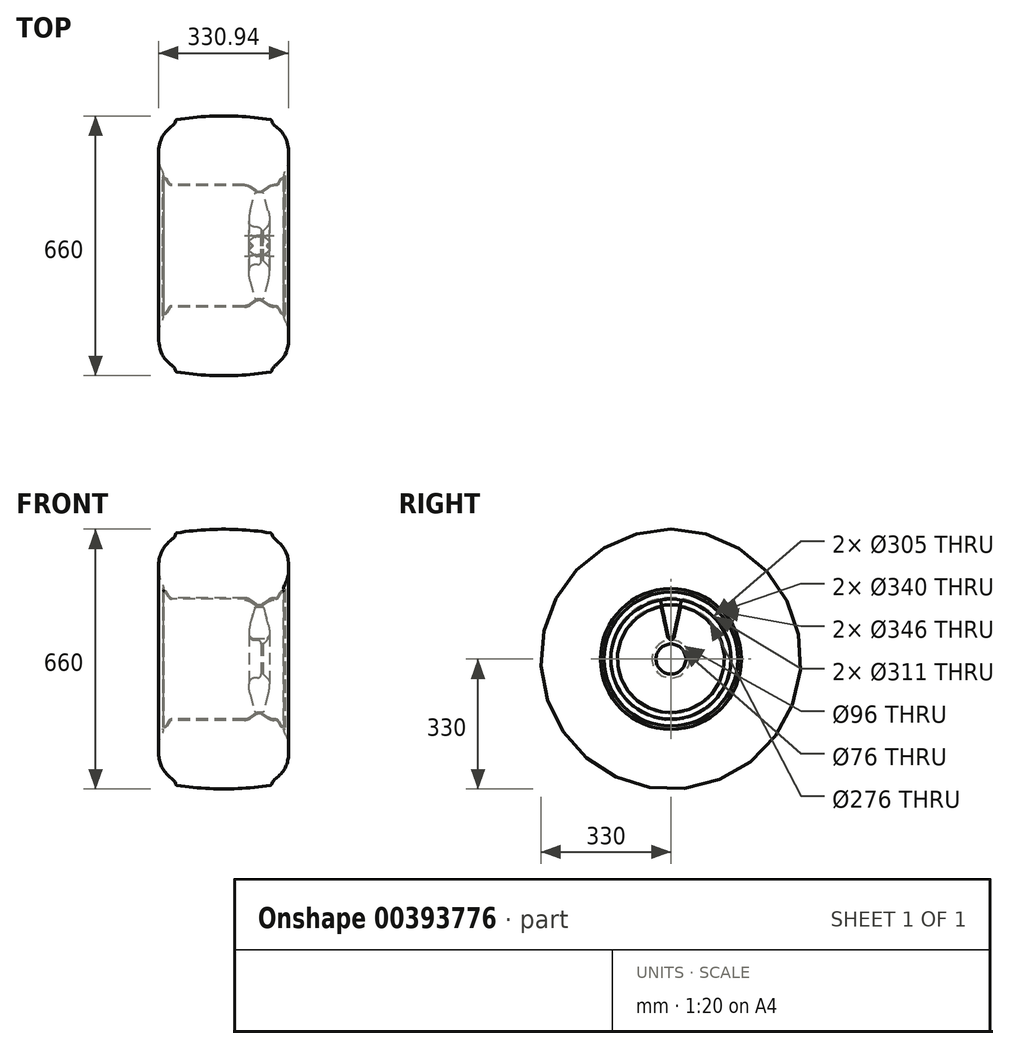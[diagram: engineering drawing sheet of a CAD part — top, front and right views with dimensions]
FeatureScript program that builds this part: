
annotation { "Feature Type Name" : "Feature", "Feature Type Description" : "" }
export const myFeature = defineFeature(function(context is Context, id is Id, definition is map)
    precondition{}
    {
        {
            var Q0;
            Q0=qCreatedBy(makeId("Front.planeOp"),FACE);
            var sketch = newSketch(context, id + "F0", { "sketchPlane" : qUnion([Q0])});
            skLineSegment(sketch, "E0", {"start": v(66.86, 147.98) * mm, "end": v(81.53, 137.71) * mm});
            skLineSegment(sketch, "E1", {"start": v(90.13, 135) * mm, "end": v(90.67, 135) * mm});
            skLineSegment(sketch, "E2", {"start": v(99.27, 137.71) * mm, "end": v(113.94, 147.98) * mm});
            skLineSegment(sketch, "E3", {"start": v(128.28, 152.5) * mm, "end": v(131.6, 152.5) * mm});
            skLineSegment(sketch, "E4", {"start": v(149.72, 170) * mm, "end": v(151.4, 170) * mm});
            skLineSegment(sketch, "E5", {"start": v(155.4, 174) * mm, "end": v(155.4, 178) * mm});
            skLineSegment(sketch, "E6", {"start": v(-149.72, 170) * mm, "end": v(-151.4, 170) * mm});
            skLineSegment(sketch, "E7", {"start": v(-155.4, 174) * mm, "end": v(-155.4, 178) * mm});
            skLineSegment(sketch, "E8", {"start": v(-131.6, 152.5) * mm, "end": v(52.52, 152.5) * mm});
            skLineSegment(sketch, "E9", {"start": v(-146.25, 167.98) * mm, "end": v(-140.28, 157.54) * mm});
            skLineSegment(sketch, "E10", {"start": v(140.28, 157.54) * mm, "end": v(146.25, 167.98) * mm});
            skPoint(sketch, "E11.visualSharp", {"position": v(155.4, 170) * mm});
            skArc(sketch, "E11.filletArc", {"start": v(151.4, 170) * mm, "mid": v(154.23, 171.17) * mm, "end": v(155.4, 174) * mm});
            skPoint(sketch, "E12.visualSharp", {"position": v(-155.4, 170) * mm});
            skArc(sketch, "E12.filletArc", {"start": v(-155.4, 174) * mm, "mid": v(-154.23, 171.17) * mm, "end": v(-151.4, 170) * mm});
            skPoint(sketch, "E13.visualSharp", {"position": v(-137.4, 152.5) * mm});
            skArc(sketch, "E13.filletArc", {"start": v(-140.28, 157.54) * mm, "mid": v(-136.62, 153.85) * mm, "end": v(-131.6, 152.5) * mm});
            skPoint(sketch, "E14.visualSharp", {"position": v(137.4, 152.5) * mm});
            skArc(sketch, "E14.filletArc", {"start": v(131.6, 152.5) * mm, "mid": v(136.62, 153.85) * mm, "end": v(140.28, 157.54) * mm});
            skPoint(sketch, "E15.visualSharp", {"position": v(-147.4, 170) * mm});
            skArc(sketch, "E15.filletArc", {"start": v(-146.25, 167.98) * mm, "mid": v(-147.71, 169.46) * mm, "end": v(-149.72, 170) * mm});
            skPoint(sketch, "E16.visualSharp", {"position": v(147.4, 170) * mm});
            skArc(sketch, "E16.filletArc", {"start": v(149.72, 170) * mm, "mid": v(147.71, 169.46) * mm, "end": v(146.25, 167.98) * mm});
            skPoint(sketch, "E17.visualSharp", {"position": v(60.4, 152.5) * mm});
            skArc(sketch, "E17.filletArc", {"start": v(66.86, 147.98) * mm, "mid": v(60.04, 151.34) * mm, "end": v(52.52, 152.5) * mm});
            skPoint(sketch, "E18.visualSharp", {"position": v(120.4, 152.5) * mm});
            skArc(sketch, "E18.filletArc", {"start": v(128.28, 152.5) * mm, "mid": v(120.76, 151.34) * mm, "end": v(113.94, 147.98) * mm});
            skPoint(sketch, "E19.visualSharp", {"position": v(95.4, 135) * mm});
            skArc(sketch, "E19.filletArc", {"start": v(90.67, 135) * mm, "mid": v(95.18, 135.7) * mm, "end": v(99.27, 137.71) * mm});
            skPoint(sketch, "E20.visualSharp", {"position": v(85.4, 135) * mm});
            skArc(sketch, "E20.filletArc", {"start": v(81.53, 137.71) * mm, "mid": v(85.62, 135.7) * mm, "end": v(90.13, 135) * mm});
            skLineSegment(sketch, "E21.0", {"start": v(152.4, 174) * mm, "end": v(152.4, 178) * mm});
            skArc(sketch, "E21.1", {"start": v(151.4, 173) * mm, "mid": v(152.1, 173.3) * mm, "end": v(152.4, 174) * mm});
            skLineSegment(sketch, "E21.2", {"start": v(149.72, 173) * mm, "end": v(151.4, 173) * mm});
            skArc(sketch, "E21.3", {"start": v(149.72, 173) * mm, "mid": v(146.2, 172.05) * mm, "end": v(143.64, 169.47) * mm});
            skLineSegment(sketch, "E21.4", {"start": v(137.67, 159.03) * mm, "end": v(143.64, 169.47) * mm});
            skArc(sketch, "E21.5", {"start": v(131.6, 155.5) * mm, "mid": v(135.11, 156.45) * mm, "end": v(137.67, 159.03) * mm});
            skLineSegment(sketch, "E21.6", {"start": v(128.28, 155.5) * mm, "end": v(131.6, 155.5) * mm});
            skArc(sketch, "E21.7", {"start": v(128.28, 155.5) * mm, "mid": v(119.86, 154.2) * mm, "end": v(112.22, 150.44) * mm});
            skLineSegment(sketch, "E21.8", {"start": v(97.55, 140.17) * mm, "end": v(112.22, 150.44) * mm});
            skArc(sketch, "E21.9", {"start": v(90.67, 138) * mm, "mid": v(94.28, 138.56) * mm, "end": v(97.55, 140.17) * mm});
            skLineSegment(sketch, "E21.10", {"start": v(90.13, 138) * mm, "end": v(90.67, 138) * mm});
            skArc(sketch, "E21.11", {"start": v(-143.64, 169.47) * mm, "mid": v(-146.2, 172.05) * mm, "end": v(-149.72, 173) * mm});
            skLineSegment(sketch, "E21.12", {"start": v(-149.72, 173) * mm, "end": v(-151.4, 173) * mm});
            skArc(sketch, "E21.13", {"start": v(-152.4, 174) * mm, "mid": v(-152.1, 173.3) * mm, "end": v(-151.4, 173) * mm});
            skLineSegment(sketch, "E21.14", {"start": v(-152.4, 174) * mm, "end": v(-152.4, 178) * mm});
            skLineSegment(sketch, "E21.15", {"start": v(-143.64, 169.47) * mm, "end": v(-137.67, 159.03) * mm});
            skArc(sketch, "E21.16", {"start": v(-137.67, 159.03) * mm, "mid": v(-135.11, 156.45) * mm, "end": v(-131.6, 155.5) * mm});
            skLineSegment(sketch, "E21.17", {"start": v(-131.6, 155.5) * mm, "end": v(52.52, 155.5) * mm});
            skArc(sketch, "E21.18", {"start": v(68.58, 150.44) * mm, "mid": v(60.94, 154.2) * mm, "end": v(52.52, 155.5) * mm});
            skLineSegment(sketch, "E21.19", {"start": v(68.58, 150.44) * mm, "end": v(83.25, 140.17) * mm});
            skArc(sketch, "E21.20", {"start": v(83.25, 140.17) * mm, "mid": v(86.52, 138.56) * mm, "end": v(90.13, 138) * mm});
            skLineSegment(sketch, "E22", {"start": v(154.4, 179) * mm, "end": v(153.4, 179) * mm});
            skLineSegment(sketch, "E23", {"start": v(-154.4, 179) * mm, "end": v(-153.4, 179) * mm});
            skPoint(sketch, "E24.visualSharp", {"position": v(-155.4, 179) * mm});
            skArc(sketch, "E24.filletArc", {"start": v(-154.4, 179) * mm, "mid": v(-155.1, 178.7) * mm, "end": v(-155.4, 178) * mm});
            skPoint(sketch, "E25.visualSharp", {"position": v(-152.4, 179) * mm});
            skArc(sketch, "E25.filletArc", {"start": v(-152.4, 178) * mm, "mid": v(-152.7, 178.7) * mm, "end": v(-153.4, 179) * mm});
            skPoint(sketch, "E26.visualSharp", {"position": v(152.4, 179) * mm});
            skArc(sketch, "E26.filletArc", {"start": v(153.4, 179) * mm, "mid": v(152.7, 178.7) * mm, "end": v(152.4, 178) * mm});
            skPoint(sketch, "E27.visualSharp", {"position": v(155.4, 179) * mm});
            skArc(sketch, "E27.filletArc", {"start": v(155.4, 178) * mm, "mid": v(155.1, 178.7) * mm, "end": v(154.4, 179) * mm});
            skLineSegment(sketch, "E28", {"start": v(-244.06, 0) * mm, "end": v(333.32, 0) * mm, "construction": true});
            skLineSegment(sketch, "E29", {"start": v(100.15, 138.32) * mm, "end": v(113.4, 88.88) * mm});
            skArc(sketch, "E30", {"start": v(113.4, 88.88) * mm, "mid": v(115.94, 76.05) * mm, "end": v(116.8, 63) * mm});
            skLineSegment(sketch, "E31", {"start": v(116.8, 63) * mm, "end": v(116.8, 94.03) * mm, "construction": true});
            skLineSegment(sketch, "E32", {"start": v(85.59, 48) * mm, "end": v(79, 48) * mm});
            skArc(sketch, "E33", {"start": v(79, 48) * mm, "mid": v(68.4, 52.4) * mm, "end": v(64, 63) * mm});
            skArc(sketch, "E34", {"start": v(64, 63) * mm, "mid": v(64.86, 76.05) * mm, "end": v(67.4, 88.88) * mm});
            skLineSegment(sketch, "E35", {"start": v(64, 63) * mm, "end": v(64, 94.03) * mm, "construction": true});
            skLineSegment(sketch, "E36", {"start": v(67.4, 88.88) * mm, "end": v(80.65, 138.32) * mm});
            skLineSegment(sketch, "E37", {"start": v(95.59, 38) * mm, "end": v(95.59, 38) * mm});
            skLineSegment(sketch, "E38", {"start": v(95.59, 38) * mm, "end": v(100.59, 38) * mm});
            skLineSegment(sketch, "E39", {"start": v(100.59, 38) * mm, "end": v(110.59, 48) * mm});
            skPoint(sketch, "E40.visualSharp", {"position": v(95.59, 48) * mm});
            skArc(sketch, "E40.filletArc", {"start": v(95.59, 38) * mm, "mid": v(92.66, 45.07) * mm, "end": v(85.59, 48) * mm});
            skArc(sketch, "E41", {"start": v(116.8, 63) * mm, "mid": v(115.19, 54.88) * mm, "end": v(110.59, 48) * mm});
            skArc(sketch, "E42", {"start": v(118.53, 320.64) * mm, "mid": v(0, 330) * mm, "end": v(-118.53, 320.64) * mm});
            skPoint(sketch, "E43.start.orphan", {"position": v(0, 330) * mm});
            skFitSpline(sketch, "E44", {"points": [v(152.4, 178) * mm, v(154.47, 187.1) * mm, v(163.17, 209.6) * mm, v(156.15, 276.43) * mm, v(126.69, 308.66) * mm, v(122.5, 320) * mm], "startDerivative": vector(0, 85.8) * mm, "endDerivative": vector(0, 123.74) * mm});
            skLineSegment(sketch, "E45", {"start": v(122.5, 320) * mm, "end": v(122.5, 293) * mm, "construction": true});
            skFitSpline(sketch, "E46", {"points": [v(-122.5, 320) * mm, v(-126.69, 308.66) * mm, v(-156.15, 276.43) * mm, v(-163.17, 209.6) * mm, v(-154.47, 187.1) * mm, v(-152.4, 178) * mm], "startDerivative": vector(0, -123.74) * mm, "endDerivative": vector(0, -85.8) * mm});
            skLineSegment(sketch, "E47", {"start": v(-122.5, 320) * mm, "end": v(-122.5, 293) * mm, "construction": true});
            skArc(sketch, "E48.filletArc", {"start": v(122.7, 316.36) * mm, "mid": v(121.32, 319.2) * mm, "end": v(118.53, 320.64) * mm});
            skArc(sketch, "E49.filletArc", {"start": v(-118.53, 320.64) * mm, "mid": v(-121.32, 319.2) * mm, "end": v(-122.7, 316.36) * mm});
            skSolve(sketch);
        }
        {
            var Q0;
            Q0=qCreatedBy(makeId("Right.planeOp"),FACE);
            var sketch = newSketch(context, id + "F1", { "sketchPlane" : qUnion([Q0])});
            skArc(sketch, "E50", {"start": v(-29.75, 149.57) * mm, "mid": v(0, 152.5) * mm, "end": v(29.75, 149.57) * mm, "construction": true});
            skLineSegment(sketch, "E51", {"start": v(-29.75, 149.57) * mm, "end": v(0, 0) * mm, "construction": true});
            skLineSegment(sketch, "E52", {"start": v(29.75, 149.57) * mm, "end": v(0, 0) * mm, "construction": true});
            skArc(sketch, "E53", {"start": v(10.34, 51.98) * mm, "mid": v(0, 53) * mm, "end": v(-10.34, 51.98) * mm, "construction": true});
            skLineSegment(sketch, "E54", {"start": v(0, 0) * mm, "end": v(-34.81, 197.43) * mm, "construction": true});
            skLineSegment(sketch, "E55", {"start": v(0, 0) * mm, "end": v(34.81, 197.43) * mm, "construction": true});
            skArc(sketch, "E56", {"start": v(26.48, 150.18) * mm, "mid": v(0, 152.5) * mm, "end": v(-26.48, 150.18) * mm});
            skLineSegment(sketch, "E57", {"start": v(0, 0) * mm, "end": v(19.74, 187.83) * mm, "construction": true});
            skLineSegment(sketch, "E58", {"start": v(0, 0) * mm, "end": v(-19.74, 187.83) * mm, "construction": true});
            skLineSegment(sketch, "E59", {"start": v(-6.78, 58.48) * mm, "end": v(-26.48, 150.18) * mm});
            skLineSegment(sketch, "E60", {"start": v(6.78, 58.48) * mm, "end": v(26.48, 150.18) * mm});
            skPoint(sketch, "E61.visualSharp", {"position": v(-5.54, 52.7) * mm});
            skArc(sketch, "E61.filletArc", {"start": v(-6.78, 58.48) * mm, "mid": v(-4.36, 54.54) * mm, "end": v(0, 53) * mm});
            skPoint(sketch, "E62.visualSharp", {"position": v(5.54, 52.7) * mm});
            skArc(sketch, "E62.filletArc", {"start": v(0, 53) * mm, "mid": v(4.36, 54.54) * mm, "end": v(6.78, 58.48) * mm});
            skSolve(sketch);
        }
        {
            var Q0;
            Q0=makeQuery(id+"F0.imprint","IMPRINT",FACE,{"disambiguationData":[TD([[makeQuery(id+"F0.imprint","IMPRINT",EDGE,{"derivedFrom":sQuery(id+"F0.wireOp",EDGE,"E3")}),1.0]])]});
            var Q1;
            Q1=sQuery(id+"F0.wireOp",EDGE,"E28");
            revolve(context, id + "F2", {"entities" : qUnion([Q0]), "axis" : qUnion([Q1]), "revolveType" : RevolveType.FULL});
        }
        {
            var Q0;
            Q0=makeQuery(id+"F0.imprint","IMPRINT",FACE,{"disambiguationData":[TD([[makeQuery(id+"F0.imprint","IMPRINT",EDGE,{"derivedFrom":sQuery(id+"F0.wireOp",EDGE,"E1")}),-1.0]])]});
            var Q1;
            Q1=sQuery(id+"F0.wireOp",EDGE,"E28");
            revolve(context, id + "F3", {"entities" : qUnion([Q0]), "axis" : qUnion([Q1]), "revolveType" : RevolveType.FULL});
        }
        {
            var Q0;
            Q0=makeQuery(id+"F1.imprint","IMPRINT",FACE,{"disambiguationData":[TD([[makeQuery(id+"F1.imprint","IMPRINT",EDGE,{"derivedFrom":sQuery(id+"F1.wireOp",EDGE,"E56")}),1.0]])]});
            extrude(context, id + "F4", {"entities" : qUnion([Q0]), "operationType" : NewBodyOperationType.REMOVE, "endBound" : BoundingType.THROUGH_ALL, "oppositeDirection" : true, "depth" : 25 * mm, "hasSecondDirection" : true, "secondDirectionBound" : SecondDirectionBoundingType.THROUGH_ALL, "secondDirectionOppositeDirection" : false, "secondDirectionDepth" : 25 * mm});
        }
        {
            var Q0;
            Q0=makeQuery(id+"F4.boolean.opBoolean","INTERSECT",EDGE,{"derivedFrom":[makeQuery(id+"F3.opRevolve","SWEPT_FACE",FACE,{"disambiguationData":[OSD([sQuery(id+"F0.wireOp",EDGE,"E34")])]}),makeQuery(id+"F4.opExtrude","SWEPT_FACE",FACE,{"disambiguationData":[OSD([sQuery(id+"F1.wireOp",EDGE,"E60")])]})]});
            var Q1;
            Q1=makeQuery(id+"F1MoAnU7Y2teXVl_2.1.F4.boolean.opBoolean","INTERSECT",EDGE,{"derivedFrom":[makeQuery(id+"F3.opRevolve","SWEPT_FACE",FACE,{"disambiguationData":[OSD([sQuery(id+"F0.wireOp",EDGE,"E34")])]}),makeQuery(id+"F1MoAnU7Y2teXVl_2.1.F4.opExtrude","SWEPT_FACE",FACE,{"disambiguationData":[OSD([sQuery(id+"F1.wireOp",EDGE,"E60")])]})]});
            var Q2;
            {var subQ0=sQuery(id+"F1.wireOp",EDGE,"E60");Q2=makeQuery(id+"F1MoAnU7Y2teXVl_2.2.F4.boolean.opBoolean","INTERSECT",EDGE,{"derivedFrom":[makeQuery(id+"F1MoAnU7Y2teXVl_2.1.F4.boolean.opBoolean","SPLIT",FACE,{"disambiguationData":[TD([makeQuery(id+"F4.boolean.opBoolean","COPY",FACE,{"derivedFrom":makeQuery(id+"F4.opExtrude","SWEPT_FACE",FACE,{"disambiguationData":[OSD([subQ0])]})})])],"derivedFrom":makeQuery(id+"F3.opRevolve","SWEPT_FACE",FACE,{"disambiguationData":[OSD([sQuery(id+"F0.wireOp",EDGE,"E34")])]})}),makeQuery(id+"F1MoAnU7Y2teXVl_2.2.F4.opExtrude","SWEPT_FACE",FACE,{"disambiguationData":[OSD([subQ0])]})]});}
            var Q3;
            {var subQ0=sQuery(id+"F1.wireOp",EDGE,"E60");var subQ3=makeQuery(id+"F4.boolean.opBoolean","COPY",FACE,{"derivedFrom":makeQuery(id+"F4.opExtrude","SWEPT_FACE",FACE,{"disambiguationData":[OSD([subQ0])]})});Q3=makeQuery(id+"F1MoAnU7Y2teXVl_2.3.F4.boolean.opBoolean","INTERSECT",EDGE,{"derivedFrom":[makeQuery(id+"F1MoAnU7Y2teXVl_2.2.F4.boolean.opBoolean","SPLIT",FACE,{"disambiguationData":[TD([subQ3])],"derivedFrom":makeQuery(id+"F1MoAnU7Y2teXVl_2.1.F4.boolean.opBoolean","SPLIT",FACE,{"disambiguationData":[TD([subQ3])],"derivedFrom":makeQuery(id+"F3.opRevolve","SWEPT_FACE",FACE,{"disambiguationData":[OSD([sQuery(id+"F0.wireOp",EDGE,"E34")])]})})}),makeQuery(id+"F1MoAnU7Y2teXVl_2.3.F4.opExtrude","SWEPT_FACE",FACE,{"disambiguationData":[OSD([subQ0])]})]});}
            var Q4;
            {var subQ0=sQuery(id+"F1.wireOp",EDGE,"E60");var subQ3=makeQuery(id+"F4.boolean.opBoolean","COPY",FACE,{"derivedFrom":makeQuery(id+"F4.opExtrude","SWEPT_FACE",FACE,{"disambiguationData":[OSD([subQ0])]})});Q4=makeQuery(id+"F1MoAnU7Y2teXVl_2.4.F4.boolean.opBoolean","INTERSECT",EDGE,{"derivedFrom":[makeQuery(id+"F1MoAnU7Y2teXVl_2.3.F4.boolean.opBoolean","SPLIT",FACE,{"disambiguationData":[TD([subQ3])],"derivedFrom":makeQuery(id+"F1MoAnU7Y2teXVl_2.2.F4.boolean.opBoolean","SPLIT",FACE,{"disambiguationData":[TD([subQ3])],"derivedFrom":makeQuery(id+"F1MoAnU7Y2teXVl_2.1.F4.boolean.opBoolean","SPLIT",FACE,{"disambiguationData":[TD([subQ3])],"derivedFrom":makeQuery(id+"F3.opRevolve","SWEPT_FACE",FACE,{"disambiguationData":[OSD([sQuery(id+"F0.wireOp",EDGE,"E34")])]})})})}),makeQuery(id+"F1MoAnU7Y2teXVl_2.4.F4.opExtrude","SWEPT_FACE",FACE,{"disambiguationData":[OSD([subQ0])]})]});}
            var Q5;
            {var subQ0=sQuery(id+"F1.wireOp",EDGE,"E60");var subQ3=makeQuery(id+"F4.boolean.opBoolean","COPY",FACE,{"derivedFrom":makeQuery(id+"F4.opExtrude","SWEPT_FACE",FACE,{"disambiguationData":[OSD([subQ0])]})});Q5=makeQuery(id+"F1MoAnU7Y2teXVl_2.5.F4.boolean.opBoolean","INTERSECT",EDGE,{"derivedFrom":[makeQuery(id+"F1MoAnU7Y2teXVl_2.4.F4.boolean.opBoolean","SPLIT",FACE,{"disambiguationData":[TD([subQ3])],"derivedFrom":makeQuery(id+"F1MoAnU7Y2teXVl_2.3.F4.boolean.opBoolean","SPLIT",FACE,{"disambiguationData":[TD([subQ3])],"derivedFrom":makeQuery(id+"F1MoAnU7Y2teXVl_2.2.F4.boolean.opBoolean","SPLIT",FACE,{"disambiguationData":[TD([subQ3])],"derivedFrom":makeQuery(id+"F1MoAnU7Y2teXVl_2.1.F4.boolean.opBoolean","SPLIT",FACE,{"disambiguationData":[TD([subQ3])],"derivedFrom":makeQuery(id+"F3.opRevolve","SWEPT_FACE",FACE,{"disambiguationData":[OSD([sQuery(id+"F0.wireOp",EDGE,"E34")])]})})})})}),makeQuery(id+"F1MoAnU7Y2teXVl_2.5.F4.opExtrude","SWEPT_FACE",FACE,{"disambiguationData":[OSD([subQ0])]})]});}
            var Q6;
            {var subQ0=sQuery(id+"F1.wireOp",EDGE,"E60");var subQ4=makeQuery(id+"F4.boolean.opBoolean","COPY",FACE,{"derivedFrom":makeQuery(id+"F4.opExtrude","SWEPT_FACE",FACE,{"disambiguationData":[OSD([subQ0])]})});Q6=makeQuery(id+"F1MoAnU7Y2teXVl_2.6.F4.boolean.opBoolean","INTERSECT",EDGE,{"derivedFrom":[makeQuery(id+"F1MoAnU7Y2teXVl_2.5.F4.boolean.opBoolean","SPLIT",FACE,{"disambiguationData":[TD([subQ4])],"derivedFrom":makeQuery(id+"F1MoAnU7Y2teXVl_2.4.F4.boolean.opBoolean","SPLIT",FACE,{"disambiguationData":[TD([subQ4])],"derivedFrom":makeQuery(id+"F1MoAnU7Y2teXVl_2.3.F4.boolean.opBoolean","SPLIT",FACE,{"disambiguationData":[TD([subQ4])],"derivedFrom":makeQuery(id+"F1MoAnU7Y2teXVl_2.2.F4.boolean.opBoolean","SPLIT",FACE,{"disambiguationData":[TD([subQ4])],"derivedFrom":makeQuery(id+"F1MoAnU7Y2teXVl_2.1.F4.boolean.opBoolean","SPLIT",FACE,{"disambiguationData":[TD([subQ4])],"derivedFrom":makeQuery(id+"F3.opRevolve","SWEPT_FACE",FACE,{"disambiguationData":[OSD([sQuery(id+"F0.wireOp",EDGE,"E34")])]})})})})})}),makeQuery(id+"F1MoAnU7Y2teXVl_2.6.F4.opExtrude","SWEPT_FACE",FACE,{"disambiguationData":[OSD([subQ0])]})]});}
            var Q7;
            {var subQ0=sQuery(id+"F1.wireOp",EDGE,"E60");var subQ3=makeQuery(id+"F4.boolean.opBoolean","COPY",FACE,{"derivedFrom":makeQuery(id+"F4.opExtrude","SWEPT_FACE",FACE,{"disambiguationData":[OSD([subQ0])]})});Q7=makeQuery(id+"F1MoAnU7Y2teXVl_2.7.F4.boolean.opBoolean","INTERSECT",EDGE,{"derivedFrom":[makeQuery(id+"F1MoAnU7Y2teXVl_2.6.F4.boolean.opBoolean","SPLIT",FACE,{"disambiguationData":[TD([subQ3])],"derivedFrom":makeQuery(id+"F1MoAnU7Y2teXVl_2.5.F4.boolean.opBoolean","SPLIT",FACE,{"disambiguationData":[TD([subQ3])],"derivedFrom":makeQuery(id+"F1MoAnU7Y2teXVl_2.4.F4.boolean.opBoolean","SPLIT",FACE,{"disambiguationData":[TD([subQ3])],"derivedFrom":makeQuery(id+"F1MoAnU7Y2teXVl_2.3.F4.boolean.opBoolean","SPLIT",FACE,{"disambiguationData":[TD([subQ3])],"derivedFrom":makeQuery(id+"F1MoAnU7Y2teXVl_2.2.F4.boolean.opBoolean","SPLIT",FACE,{"disambiguationData":[TD([subQ3])],"derivedFrom":makeQuery(id+"F1MoAnU7Y2teXVl_2.1.F4.boolean.opBoolean","SPLIT",FACE,{"disambiguationData":[TD([subQ3])],"derivedFrom":makeQuery(id+"F3.opRevolve","SWEPT_FACE",FACE,{"disambiguationData":[OSD([sQuery(id+"F0.wireOp",EDGE,"E34")])]})})})})})})}),makeQuery(id+"F1MoAnU7Y2teXVl_2.7.F4.opExtrude","SWEPT_FACE",FACE,{"disambiguationData":[OSD([subQ0])]})]});}
            var Q8;
            {var subQ0=sQuery(id+"F1.wireOp",EDGE,"E60");var subQ3=makeQuery(id+"F4.boolean.opBoolean","COPY",FACE,{"derivedFrom":makeQuery(id+"F4.opExtrude","SWEPT_FACE",FACE,{"disambiguationData":[OSD([subQ0])]})});Q8=makeQuery(id+"F1MoAnU7Y2teXVl_2.8.F4.boolean.opBoolean","INTERSECT",EDGE,{"derivedFrom":[makeQuery(id+"F1MoAnU7Y2teXVl_2.7.F4.boolean.opBoolean","SPLIT",FACE,{"disambiguationData":[TD([subQ3])],"derivedFrom":makeQuery(id+"F1MoAnU7Y2teXVl_2.6.F4.boolean.opBoolean","SPLIT",FACE,{"disambiguationData":[TD([subQ3])],"derivedFrom":makeQuery(id+"F1MoAnU7Y2teXVl_2.5.F4.boolean.opBoolean","SPLIT",FACE,{"disambiguationData":[TD([subQ3])],"derivedFrom":makeQuery(id+"F1MoAnU7Y2teXVl_2.4.F4.boolean.opBoolean","SPLIT",FACE,{"disambiguationData":[TD([subQ3])],"derivedFrom":makeQuery(id+"F1MoAnU7Y2teXVl_2.3.F4.boolean.opBoolean","SPLIT",FACE,{"disambiguationData":[TD([subQ3])],"derivedFrom":makeQuery(id+"F1MoAnU7Y2teXVl_2.2.F4.boolean.opBoolean","SPLIT",FACE,{"disambiguationData":[TD([subQ3])],"derivedFrom":makeQuery(id+"F1MoAnU7Y2teXVl_2.1.F4.boolean.opBoolean","SPLIT",FACE,{"disambiguationData":[TD([subQ3])],"derivedFrom":makeQuery(id+"F3.opRevolve","SWEPT_FACE",FACE,{"disambiguationData":[OSD([sQuery(id+"F0.wireOp",EDGE,"E34")])]})})})})})})})}),makeQuery(id+"F1MoAnU7Y2teXVl_2.8.F4.opExtrude","SWEPT_FACE",FACE,{"disambiguationData":[OSD([subQ0])]})]});}
            var Q9;
            {var subQ0=sQuery(id+"F1.wireOp",EDGE,"E60");var subQ3=makeQuery(id+"F4.boolean.opBoolean","COPY",FACE,{"derivedFrom":makeQuery(id+"F4.opExtrude","SWEPT_FACE",FACE,{"disambiguationData":[OSD([subQ0])]})});Q9=makeQuery(id+"F1MoAnU7Y2teXVl_2.9.F4.boolean.opBoolean","INTERSECT",EDGE,{"derivedFrom":[makeQuery(id+"F1MoAnU7Y2teXVl_2.8.F4.boolean.opBoolean","SPLIT",FACE,{"disambiguationData":[TD([subQ3])],"derivedFrom":makeQuery(id+"F1MoAnU7Y2teXVl_2.7.F4.boolean.opBoolean","SPLIT",FACE,{"disambiguationData":[TD([subQ3])],"derivedFrom":makeQuery(id+"F1MoAnU7Y2teXVl_2.6.F4.boolean.opBoolean","SPLIT",FACE,{"disambiguationData":[TD([subQ3])],"derivedFrom":makeQuery(id+"F1MoAnU7Y2teXVl_2.5.F4.boolean.opBoolean","SPLIT",FACE,{"disambiguationData":[TD([subQ3])],"derivedFrom":makeQuery(id+"F1MoAnU7Y2teXVl_2.4.F4.boolean.opBoolean","SPLIT",FACE,{"disambiguationData":[TD([subQ3])],"derivedFrom":makeQuery(id+"F1MoAnU7Y2teXVl_2.3.F4.boolean.opBoolean","SPLIT",FACE,{"disambiguationData":[TD([subQ3])],"derivedFrom":makeQuery(id+"F1MoAnU7Y2teXVl_2.2.F4.boolean.opBoolean","SPLIT",FACE,{"disambiguationData":[TD([subQ3])],"derivedFrom":makeQuery(id+"F1MoAnU7Y2teXVl_2.1.F4.boolean.opBoolean","SPLIT",FACE,{"disambiguationData":[TD([subQ3])],"derivedFrom":makeQuery(id+"F3.opRevolve","SWEPT_FACE",FACE,{"disambiguationData":[OSD([sQuery(id+"F0.wireOp",EDGE,"E34")])]})})})})})})})})}),makeQuery(id+"F1MoAnU7Y2teXVl_2.9.F4.opExtrude","SWEPT_FACE",FACE,{"disambiguationData":[OSD([subQ0])]})]});}
            var Q10;
            {var subQ0=sQuery(id+"F1.wireOp",EDGE,"E60");var subQ4=makeQuery(id+"F4.boolean.opBoolean","COPY",FACE,{"derivedFrom":makeQuery(id+"F4.opExtrude","SWEPT_FACE",FACE,{"disambiguationData":[OSD([subQ0])]})});Q10=makeQuery(id+"F1MoAnU7Y2teXVl_2.10.F4.boolean.opBoolean","INTERSECT",EDGE,{"derivedFrom":[makeQuery(id+"F1MoAnU7Y2teXVl_2.9.F4.boolean.opBoolean","SPLIT",FACE,{"disambiguationData":[TD([subQ4])],"derivedFrom":makeQuery(id+"F1MoAnU7Y2teXVl_2.8.F4.boolean.opBoolean","SPLIT",FACE,{"disambiguationData":[TD([subQ4])],"derivedFrom":makeQuery(id+"F1MoAnU7Y2teXVl_2.7.F4.boolean.opBoolean","SPLIT",FACE,{"disambiguationData":[TD([subQ4])],"derivedFrom":makeQuery(id+"F1MoAnU7Y2teXVl_2.6.F4.boolean.opBoolean","SPLIT",FACE,{"disambiguationData":[TD([subQ4])],"derivedFrom":makeQuery(id+"F1MoAnU7Y2teXVl_2.5.F4.boolean.opBoolean","SPLIT",FACE,{"disambiguationData":[TD([subQ4])],"derivedFrom":makeQuery(id+"F1MoAnU7Y2teXVl_2.4.F4.boolean.opBoolean","SPLIT",FACE,{"disambiguationData":[TD([subQ4])],"derivedFrom":makeQuery(id+"F1MoAnU7Y2teXVl_2.3.F4.boolean.opBoolean","SPLIT",FACE,{"disambiguationData":[TD([subQ4])],"derivedFrom":makeQuery(id+"F1MoAnU7Y2teXVl_2.2.F4.boolean.opBoolean","SPLIT",FACE,{"disambiguationData":[TD([subQ4])],"derivedFrom":makeQuery(id+"F1MoAnU7Y2teXVl_2.1.F4.boolean.opBoolean","SPLIT",FACE,{"disambiguationData":[TD([subQ4])],"derivedFrom":makeQuery(id+"F3.opRevolve","SWEPT_FACE",FACE,{"disambiguationData":[OSD([sQuery(id+"F0.wireOp",EDGE,"E34")])]})})})})})})})})})}),makeQuery(id+"F1MoAnU7Y2teXVl_2.10.F4.opExtrude","SWEPT_FACE",FACE,{"disambiguationData":[OSD([subQ0])]})]});}
            var Q11;
            {var subQ0=sQuery(id+"F1.wireOp",EDGE,"E60");var subQ3=makeQuery(id+"F4.boolean.opBoolean","COPY",FACE,{"derivedFrom":makeQuery(id+"F4.opExtrude","SWEPT_FACE",FACE,{"disambiguationData":[OSD([subQ0])]})});Q11=makeQuery(id+"F1MoAnU7Y2teXVl_2.11.F4.boolean.opBoolean","INTERSECT",EDGE,{"derivedFrom":[makeQuery(id+"F1MoAnU7Y2teXVl_2.10.F4.boolean.opBoolean","SPLIT",FACE,{"disambiguationData":[TD([subQ3])],"derivedFrom":makeQuery(id+"F1MoAnU7Y2teXVl_2.9.F4.boolean.opBoolean","SPLIT",FACE,{"disambiguationData":[TD([subQ3])],"derivedFrom":makeQuery(id+"F1MoAnU7Y2teXVl_2.8.F4.boolean.opBoolean","SPLIT",FACE,{"disambiguationData":[TD([subQ3])],"derivedFrom":makeQuery(id+"F1MoAnU7Y2teXVl_2.7.F4.boolean.opBoolean","SPLIT",FACE,{"disambiguationData":[TD([subQ3])],"derivedFrom":makeQuery(id+"F1MoAnU7Y2teXVl_2.6.F4.boolean.opBoolean","SPLIT",FACE,{"disambiguationData":[TD([subQ3])],"derivedFrom":makeQuery(id+"F1MoAnU7Y2teXVl_2.5.F4.boolean.opBoolean","SPLIT",FACE,{"disambiguationData":[TD([subQ3])],"derivedFrom":makeQuery(id+"F1MoAnU7Y2teXVl_2.4.F4.boolean.opBoolean","SPLIT",FACE,{"disambiguationData":[TD([subQ3])],"derivedFrom":makeQuery(id+"F1MoAnU7Y2teXVl_2.3.F4.boolean.opBoolean","SPLIT",FACE,{"disambiguationData":[TD([subQ3])],"derivedFrom":makeQuery(id+"F1MoAnU7Y2teXVl_2.2.F4.boolean.opBoolean","SPLIT",FACE,{"disambiguationData":[TD([subQ3])],"derivedFrom":makeQuery(id+"F1MoAnU7Y2teXVl_2.1.F4.boolean.opBoolean","SPLIT",FACE,{"disambiguationData":[TD([subQ3])],"derivedFrom":makeQuery(id+"F3.opRevolve","SWEPT_FACE",FACE,{"disambiguationData":[OSD([sQuery(id+"F0.wireOp",EDGE,"E34")])]})})})})})})})})})})}),makeQuery(id+"F1MoAnU7Y2teXVl_2.11.F4.opExtrude","SWEPT_FACE",FACE,{"disambiguationData":[OSD([subQ0])]})]});}
            var Q12;
            {var subQ0=sQuery(id+"F1.wireOp",EDGE,"E60");var subQ3=makeQuery(id+"F4.boolean.opBoolean","COPY",FACE,{"derivedFrom":makeQuery(id+"F4.opExtrude","SWEPT_FACE",FACE,{"disambiguationData":[OSD([subQ0])]})});Q12=makeQuery(id+"F1MoAnU7Y2teXVl_2.12.F4.boolean.opBoolean","INTERSECT",EDGE,{"derivedFrom":[makeQuery(id+"F1MoAnU7Y2teXVl_2.11.F4.boolean.opBoolean","SPLIT",FACE,{"disambiguationData":[TD([subQ3])],"derivedFrom":makeQuery(id+"F1MoAnU7Y2teXVl_2.10.F4.boolean.opBoolean","SPLIT",FACE,{"disambiguationData":[TD([subQ3])],"derivedFrom":makeQuery(id+"F1MoAnU7Y2teXVl_2.9.F4.boolean.opBoolean","SPLIT",FACE,{"disambiguationData":[TD([subQ3])],"derivedFrom":makeQuery(id+"F1MoAnU7Y2teXVl_2.8.F4.boolean.opBoolean","SPLIT",FACE,{"disambiguationData":[TD([subQ3])],"derivedFrom":makeQuery(id+"F1MoAnU7Y2teXVl_2.7.F4.boolean.opBoolean","SPLIT",FACE,{"disambiguationData":[TD([subQ3])],"derivedFrom":makeQuery(id+"F1MoAnU7Y2teXVl_2.6.F4.boolean.opBoolean","SPLIT",FACE,{"disambiguationData":[TD([subQ3])],"derivedFrom":makeQuery(id+"F1MoAnU7Y2teXVl_2.5.F4.boolean.opBoolean","SPLIT",FACE,{"disambiguationData":[TD([subQ3])],"derivedFrom":makeQuery(id+"F1MoAnU7Y2teXVl_2.4.F4.boolean.opBoolean","SPLIT",FACE,{"disambiguationData":[TD([subQ3])],"derivedFrom":makeQuery(id+"F1MoAnU7Y2teXVl_2.3.F4.boolean.opBoolean","SPLIT",FACE,{"disambiguationData":[TD([subQ3])],"derivedFrom":makeQuery(id+"F1MoAnU7Y2teXVl_2.2.F4.boolean.opBoolean","SPLIT",FACE,{"disambiguationData":[TD([subQ3])],"derivedFrom":makeQuery(id+"F1MoAnU7Y2teXVl_2.1.F4.boolean.opBoolean","SPLIT",FACE,{"disambiguationData":[TD([subQ3])],"derivedFrom":makeQuery(id+"F3.opRevolve","SWEPT_FACE",FACE,{"disambiguationData":[OSD([sQuery(id+"F0.wireOp",EDGE,"E34")])]})})})})})})})})})})})}),makeQuery(id+"F1MoAnU7Y2teXVl_2.12.F4.opExtrude","SWEPT_FACE",FACE,{"disambiguationData":[OSD([subQ0])]})]});}
            var Q13;
            {var subQ0=sQuery(id+"F1.wireOp",EDGE,"E60");var subQ3=makeQuery(id+"F4.boolean.opBoolean","COPY",FACE,{"derivedFrom":makeQuery(id+"F4.opExtrude","SWEPT_FACE",FACE,{"disambiguationData":[OSD([subQ0])]})});Q13=makeQuery(id+"F1MoAnU7Y2teXVl_2.13.F4.boolean.opBoolean","INTERSECT",EDGE,{"derivedFrom":[makeQuery(id+"F1MoAnU7Y2teXVl_2.12.F4.boolean.opBoolean","SPLIT",FACE,{"disambiguationData":[TD([subQ3])],"derivedFrom":makeQuery(id+"F1MoAnU7Y2teXVl_2.11.F4.boolean.opBoolean","SPLIT",FACE,{"disambiguationData":[TD([subQ3])],"derivedFrom":makeQuery(id+"F1MoAnU7Y2teXVl_2.10.F4.boolean.opBoolean","SPLIT",FACE,{"disambiguationData":[TD([subQ3])],"derivedFrom":makeQuery(id+"F1MoAnU7Y2teXVl_2.9.F4.boolean.opBoolean","SPLIT",FACE,{"disambiguationData":[TD([subQ3])],"derivedFrom":makeQuery(id+"F1MoAnU7Y2teXVl_2.8.F4.boolean.opBoolean","SPLIT",FACE,{"disambiguationData":[TD([subQ3])],"derivedFrom":makeQuery(id+"F1MoAnU7Y2teXVl_2.7.F4.boolean.opBoolean","SPLIT",FACE,{"disambiguationData":[TD([subQ3])],"derivedFrom":makeQuery(id+"F1MoAnU7Y2teXVl_2.6.F4.boolean.opBoolean","SPLIT",FACE,{"disambiguationData":[TD([subQ3])],"derivedFrom":makeQuery(id+"F1MoAnU7Y2teXVl_2.5.F4.boolean.opBoolean","SPLIT",FACE,{"disambiguationData":[TD([subQ3])],"derivedFrom":makeQuery(id+"F1MoAnU7Y2teXVl_2.4.F4.boolean.opBoolean","SPLIT",FACE,{"disambiguationData":[TD([subQ3])],"derivedFrom":makeQuery(id+"F1MoAnU7Y2teXVl_2.3.F4.boolean.opBoolean","SPLIT",FACE,{"disambiguationData":[TD([subQ3])],"derivedFrom":makeQuery(id+"F1MoAnU7Y2teXVl_2.2.F4.boolean.opBoolean","SPLIT",FACE,{"disambiguationData":[TD([subQ3])],"derivedFrom":makeQuery(id+"F1MoAnU7Y2teXVl_2.1.F4.boolean.opBoolean","SPLIT",FACE,{"disambiguationData":[TD([subQ3])],"derivedFrom":makeQuery(id+"F3.opRevolve","SWEPT_FACE",FACE,{"disambiguationData":[OSD([sQuery(id+"F0.wireOp",EDGE,"E34")])]})})})})})})})})})})})})}),makeQuery(id+"F1MoAnU7Y2teXVl_2.13.F4.opExtrude","SWEPT_FACE",FACE,{"disambiguationData":[OSD([subQ0])]})]});}
            var Q14;
            {var subQ0=sQuery(id+"F1.wireOp",EDGE,"E60");var subQ4=makeQuery(id+"F4.boolean.opBoolean","COPY",FACE,{"derivedFrom":makeQuery(id+"F4.opExtrude","SWEPT_FACE",FACE,{"disambiguationData":[OSD([subQ0])]})});Q14=makeQuery(id+"F1MoAnU7Y2teXVl_2.14.F4.boolean.opBoolean","INTERSECT",EDGE,{"derivedFrom":[makeQuery(id+"F1MoAnU7Y2teXVl_2.13.F4.boolean.opBoolean","SPLIT",FACE,{"disambiguationData":[TD([subQ4])],"derivedFrom":makeQuery(id+"F1MoAnU7Y2teXVl_2.12.F4.boolean.opBoolean","SPLIT",FACE,{"disambiguationData":[TD([subQ4])],"derivedFrom":makeQuery(id+"F1MoAnU7Y2teXVl_2.11.F4.boolean.opBoolean","SPLIT",FACE,{"disambiguationData":[TD([subQ4])],"derivedFrom":makeQuery(id+"F1MoAnU7Y2teXVl_2.10.F4.boolean.opBoolean","SPLIT",FACE,{"disambiguationData":[TD([subQ4])],"derivedFrom":makeQuery(id+"F1MoAnU7Y2teXVl_2.9.F4.boolean.opBoolean","SPLIT",FACE,{"disambiguationData":[TD([subQ4])],"derivedFrom":makeQuery(id+"F1MoAnU7Y2teXVl_2.8.F4.boolean.opBoolean","SPLIT",FACE,{"disambiguationData":[TD([subQ4])],"derivedFrom":makeQuery(id+"F1MoAnU7Y2teXVl_2.7.F4.boolean.opBoolean","SPLIT",FACE,{"disambiguationData":[TD([subQ4])],"derivedFrom":makeQuery(id+"F1MoAnU7Y2teXVl_2.6.F4.boolean.opBoolean","SPLIT",FACE,{"disambiguationData":[TD([subQ4])],"derivedFrom":makeQuery(id+"F1MoAnU7Y2teXVl_2.5.F4.boolean.opBoolean","SPLIT",FACE,{"disambiguationData":[TD([subQ4])],"derivedFrom":makeQuery(id+"F1MoAnU7Y2teXVl_2.4.F4.boolean.opBoolean","SPLIT",FACE,{"disambiguationData":[TD([subQ4])],"derivedFrom":makeQuery(id+"F1MoAnU7Y2teXVl_2.3.F4.boolean.opBoolean","SPLIT",FACE,{"disambiguationData":[TD([subQ4])],"derivedFrom":makeQuery(id+"F1MoAnU7Y2teXVl_2.2.F4.boolean.opBoolean","SPLIT",FACE,{"disambiguationData":[TD([subQ4])],"derivedFrom":makeQuery(id+"F1MoAnU7Y2teXVl_2.1.F4.boolean.opBoolean","SPLIT",FACE,{"disambiguationData":[TD([subQ4])],"derivedFrom":makeQuery(id+"F3.opRevolve","SWEPT_FACE",FACE,{"disambiguationData":[OSD([sQuery(id+"F0.wireOp",EDGE,"E34")])]})})})})})})})})})})})})})}),makeQuery(id+"F1MoAnU7Y2teXVl_2.14.F4.opExtrude","SWEPT_FACE",FACE,{"disambiguationData":[OSD([subQ0])]})]});}
            var Q15;
            {var subQ0=sQuery(id+"F1.wireOp",EDGE,"E60");var subQ3=makeQuery(id+"F4.boolean.opBoolean","COPY",FACE,{"derivedFrom":makeQuery(id+"F4.opExtrude","SWEPT_FACE",FACE,{"disambiguationData":[OSD([subQ0])]})});Q15=makeQuery(id+"F1MoAnU7Y2teXVl_2.15.F4.boolean.opBoolean","INTERSECT",EDGE,{"derivedFrom":[makeQuery(id+"F1MoAnU7Y2teXVl_2.14.F4.boolean.opBoolean","SPLIT",FACE,{"disambiguationData":[TD([subQ3])],"derivedFrom":makeQuery(id+"F1MoAnU7Y2teXVl_2.13.F4.boolean.opBoolean","SPLIT",FACE,{"disambiguationData":[TD([subQ3])],"derivedFrom":makeQuery(id+"F1MoAnU7Y2teXVl_2.12.F4.boolean.opBoolean","SPLIT",FACE,{"disambiguationData":[TD([subQ3])],"derivedFrom":makeQuery(id+"F1MoAnU7Y2teXVl_2.11.F4.boolean.opBoolean","SPLIT",FACE,{"disambiguationData":[TD([subQ3])],"derivedFrom":makeQuery(id+"F1MoAnU7Y2teXVl_2.10.F4.boolean.opBoolean","SPLIT",FACE,{"disambiguationData":[TD([subQ3])],"derivedFrom":makeQuery(id+"F1MoAnU7Y2teXVl_2.9.F4.boolean.opBoolean","SPLIT",FACE,{"disambiguationData":[TD([subQ3])],"derivedFrom":makeQuery(id+"F1MoAnU7Y2teXVl_2.8.F4.boolean.opBoolean","SPLIT",FACE,{"disambiguationData":[TD([subQ3])],"derivedFrom":makeQuery(id+"F1MoAnU7Y2teXVl_2.7.F4.boolean.opBoolean","SPLIT",FACE,{"disambiguationData":[TD([subQ3])],"derivedFrom":makeQuery(id+"F1MoAnU7Y2teXVl_2.6.F4.boolean.opBoolean","SPLIT",FACE,{"disambiguationData":[TD([subQ3])],"derivedFrom":makeQuery(id+"F1MoAnU7Y2teXVl_2.5.F4.boolean.opBoolean","SPLIT",FACE,{"disambiguationData":[TD([subQ3])],"derivedFrom":makeQuery(id+"F1MoAnU7Y2teXVl_2.4.F4.boolean.opBoolean","SPLIT",FACE,{"disambiguationData":[TD([subQ3])],"derivedFrom":makeQuery(id+"F1MoAnU7Y2teXVl_2.3.F4.boolean.opBoolean","SPLIT",FACE,{"disambiguationData":[TD([subQ3])],"derivedFrom":makeQuery(id+"F1MoAnU7Y2teXVl_2.2.F4.boolean.opBoolean","SPLIT",FACE,{"disambiguationData":[TD([subQ3])],"derivedFrom":makeQuery(id+"F1MoAnU7Y2teXVl_2.1.F4.boolean.opBoolean","SPLIT",FACE,{"disambiguationData":[TD([subQ3])],"derivedFrom":makeQuery(id+"F3.opRevolve","SWEPT_FACE",FACE,{"disambiguationData":[OSD([sQuery(id+"F0.wireOp",EDGE,"E34")])]})})})})})})})})})})})})})})}),makeQuery(id+"F1MoAnU7Y2teXVl_2.15.F4.opExtrude","SWEPT_FACE",FACE,{"disambiguationData":[OSD([subQ0])]})]});}
            var Q16;
            {var subQ0=sQuery(id+"F1.wireOp",EDGE,"E59");Q16=makeQuery(id+"F1MoAnU7Y2teXVl_2.2.F4.boolean.opBoolean","INTERSECT",EDGE,{"derivedFrom":[makeQuery(id+"F1MoAnU7Y2teXVl_2.1.F4.boolean.opBoolean","SPLIT",FACE,{"disambiguationData":[TD([makeQuery(id+"F4.boolean.opBoolean","COPY",FACE,{"derivedFrom":makeQuery(id+"F4.opExtrude","SWEPT_FACE",FACE,{"disambiguationData":[OSD([sQuery(id+"F1.wireOp",EDGE,"E60")])]})})])],"derivedFrom":makeQuery(id+"F3.opRevolve","SWEPT_FACE",FACE,{"disambiguationData":[OSD([sQuery(id+"F0.wireOp",EDGE,"E30")])]})}),makeQuery(id+"F1MoAnU7Y2teXVl_2.2.F4.opExtrude","SWEPT_FACE",FACE,{"disambiguationData":[OSD([subQ0])]})]});}
            var Q17;
            Q17=makeQuery(id+"F1MoAnU7Y2teXVl_2.1.F4.boolean.opBoolean","INTERSECT",EDGE,{"derivedFrom":[makeQuery(id+"F3.opRevolve","SWEPT_FACE",FACE,{"disambiguationData":[OSD([sQuery(id+"F0.wireOp",EDGE,"E30")])]}),makeQuery(id+"F1MoAnU7Y2teXVl_2.1.F4.opExtrude","SWEPT_FACE",FACE,{"disambiguationData":[OSD([sQuery(id+"F1.wireOp",EDGE,"E59")])]})]});
            var Q18;
            Q18=makeQuery(id+"F4.boolean.opBoolean","INTERSECT",EDGE,{"derivedFrom":[makeQuery(id+"F3.opRevolve","SWEPT_FACE",FACE,{"disambiguationData":[OSD([sQuery(id+"F0.wireOp",EDGE,"E30")])]}),makeQuery(id+"F4.opExtrude","SWEPT_FACE",FACE,{"disambiguationData":[OSD([sQuery(id+"F1.wireOp",EDGE,"E59")])]})]});
            var Q19;
            {var subQ0=sQuery(id+"F1.wireOp",EDGE,"E59");var subQ3=makeQuery(id+"F4.boolean.opBoolean","COPY",FACE,{"derivedFrom":makeQuery(id+"F4.opExtrude","SWEPT_FACE",FACE,{"disambiguationData":[OSD([sQuery(id+"F1.wireOp",EDGE,"E60")])]})});Q19=makeQuery(id+"F1MoAnU7Y2teXVl_2.15.F4.boolean.opBoolean","INTERSECT",EDGE,{"derivedFrom":[makeQuery(id+"F1MoAnU7Y2teXVl_2.14.F4.boolean.opBoolean","SPLIT",FACE,{"disambiguationData":[TD([subQ3])],"derivedFrom":makeQuery(id+"F1MoAnU7Y2teXVl_2.13.F4.boolean.opBoolean","SPLIT",FACE,{"disambiguationData":[TD([subQ3])],"derivedFrom":makeQuery(id+"F1MoAnU7Y2teXVl_2.12.F4.boolean.opBoolean","SPLIT",FACE,{"disambiguationData":[TD([subQ3])],"derivedFrom":makeQuery(id+"F1MoAnU7Y2teXVl_2.11.F4.boolean.opBoolean","SPLIT",FACE,{"disambiguationData":[TD([subQ3])],"derivedFrom":makeQuery(id+"F1MoAnU7Y2teXVl_2.10.F4.boolean.opBoolean","SPLIT",FACE,{"disambiguationData":[TD([subQ3])],"derivedFrom":makeQuery(id+"F1MoAnU7Y2teXVl_2.9.F4.boolean.opBoolean","SPLIT",FACE,{"disambiguationData":[TD([subQ3])],"derivedFrom":makeQuery(id+"F1MoAnU7Y2teXVl_2.8.F4.boolean.opBoolean","SPLIT",FACE,{"disambiguationData":[TD([subQ3])],"derivedFrom":makeQuery(id+"F1MoAnU7Y2teXVl_2.7.F4.boolean.opBoolean","SPLIT",FACE,{"disambiguationData":[TD([subQ3])],"derivedFrom":makeQuery(id+"F1MoAnU7Y2teXVl_2.6.F4.boolean.opBoolean","SPLIT",FACE,{"disambiguationData":[TD([subQ3])],"derivedFrom":makeQuery(id+"F1MoAnU7Y2teXVl_2.5.F4.boolean.opBoolean","SPLIT",FACE,{"disambiguationData":[TD([subQ3])],"derivedFrom":makeQuery(id+"F1MoAnU7Y2teXVl_2.4.F4.boolean.opBoolean","SPLIT",FACE,{"disambiguationData":[TD([subQ3])],"derivedFrom":makeQuery(id+"F1MoAnU7Y2teXVl_2.3.F4.boolean.opBoolean","SPLIT",FACE,{"disambiguationData":[TD([subQ3])],"derivedFrom":makeQuery(id+"F1MoAnU7Y2teXVl_2.2.F4.boolean.opBoolean","SPLIT",FACE,{"disambiguationData":[TD([subQ3])],"derivedFrom":makeQuery(id+"F1MoAnU7Y2teXVl_2.1.F4.boolean.opBoolean","SPLIT",FACE,{"disambiguationData":[TD([subQ3])],"derivedFrom":makeQuery(id+"F3.opRevolve","SWEPT_FACE",FACE,{"disambiguationData":[OSD([sQuery(id+"F0.wireOp",EDGE,"E30")])]})})})})})})})})})})})})})})}),makeQuery(id+"F1MoAnU7Y2teXVl_2.15.F4.opExtrude","SWEPT_FACE",FACE,{"disambiguationData":[OSD([subQ0])]})]});}
            var Q20;
            {var subQ0=sQuery(id+"F1.wireOp",EDGE,"E59");var subQ3=makeQuery(id+"F4.boolean.opBoolean","COPY",FACE,{"derivedFrom":makeQuery(id+"F4.opExtrude","SWEPT_FACE",FACE,{"disambiguationData":[OSD([sQuery(id+"F1.wireOp",EDGE,"E60")])]})});Q20=makeQuery(id+"F1MoAnU7Y2teXVl_2.14.F4.boolean.opBoolean","INTERSECT",EDGE,{"derivedFrom":[makeQuery(id+"F1MoAnU7Y2teXVl_2.13.F4.boolean.opBoolean","SPLIT",FACE,{"disambiguationData":[TD([subQ3])],"derivedFrom":makeQuery(id+"F1MoAnU7Y2teXVl_2.12.F4.boolean.opBoolean","SPLIT",FACE,{"disambiguationData":[TD([subQ3])],"derivedFrom":makeQuery(id+"F1MoAnU7Y2teXVl_2.11.F4.boolean.opBoolean","SPLIT",FACE,{"disambiguationData":[TD([subQ3])],"derivedFrom":makeQuery(id+"F1MoAnU7Y2teXVl_2.10.F4.boolean.opBoolean","SPLIT",FACE,{"disambiguationData":[TD([subQ3])],"derivedFrom":makeQuery(id+"F1MoAnU7Y2teXVl_2.9.F4.boolean.opBoolean","SPLIT",FACE,{"disambiguationData":[TD([subQ3])],"derivedFrom":makeQuery(id+"F1MoAnU7Y2teXVl_2.8.F4.boolean.opBoolean","SPLIT",FACE,{"disambiguationData":[TD([subQ3])],"derivedFrom":makeQuery(id+"F1MoAnU7Y2teXVl_2.7.F4.boolean.opBoolean","SPLIT",FACE,{"disambiguationData":[TD([subQ3])],"derivedFrom":makeQuery(id+"F1MoAnU7Y2teXVl_2.6.F4.boolean.opBoolean","SPLIT",FACE,{"disambiguationData":[TD([subQ3])],"derivedFrom":makeQuery(id+"F1MoAnU7Y2teXVl_2.5.F4.boolean.opBoolean","SPLIT",FACE,{"disambiguationData":[TD([subQ3])],"derivedFrom":makeQuery(id+"F1MoAnU7Y2teXVl_2.4.F4.boolean.opBoolean","SPLIT",FACE,{"disambiguationData":[TD([subQ3])],"derivedFrom":makeQuery(id+"F1MoAnU7Y2teXVl_2.3.F4.boolean.opBoolean","SPLIT",FACE,{"disambiguationData":[TD([subQ3])],"derivedFrom":makeQuery(id+"F1MoAnU7Y2teXVl_2.2.F4.boolean.opBoolean","SPLIT",FACE,{"disambiguationData":[TD([subQ3])],"derivedFrom":makeQuery(id+"F1MoAnU7Y2teXVl_2.1.F4.boolean.opBoolean","SPLIT",FACE,{"disambiguationData":[TD([subQ3])],"derivedFrom":makeQuery(id+"F3.opRevolve","SWEPT_FACE",FACE,{"disambiguationData":[OSD([sQuery(id+"F0.wireOp",EDGE,"E30")])]})})})})})})})})})})})})})}),makeQuery(id+"F1MoAnU7Y2teXVl_2.14.F4.opExtrude","SWEPT_FACE",FACE,{"disambiguationData":[OSD([subQ0])]})]});}
            var Q21;
            {var subQ0=sQuery(id+"F1.wireOp",EDGE,"E59");var subQ3=makeQuery(id+"F4.boolean.opBoolean","COPY",FACE,{"derivedFrom":makeQuery(id+"F4.opExtrude","SWEPT_FACE",FACE,{"disambiguationData":[OSD([sQuery(id+"F1.wireOp",EDGE,"E60")])]})});Q21=makeQuery(id+"F1MoAnU7Y2teXVl_2.13.F4.boolean.opBoolean","INTERSECT",EDGE,{"derivedFrom":[makeQuery(id+"F1MoAnU7Y2teXVl_2.12.F4.boolean.opBoolean","SPLIT",FACE,{"disambiguationData":[TD([subQ3])],"derivedFrom":makeQuery(id+"F1MoAnU7Y2teXVl_2.11.F4.boolean.opBoolean","SPLIT",FACE,{"disambiguationData":[TD([subQ3])],"derivedFrom":makeQuery(id+"F1MoAnU7Y2teXVl_2.10.F4.boolean.opBoolean","SPLIT",FACE,{"disambiguationData":[TD([subQ3])],"derivedFrom":makeQuery(id+"F1MoAnU7Y2teXVl_2.9.F4.boolean.opBoolean","SPLIT",FACE,{"disambiguationData":[TD([subQ3])],"derivedFrom":makeQuery(id+"F1MoAnU7Y2teXVl_2.8.F4.boolean.opBoolean","SPLIT",FACE,{"disambiguationData":[TD([subQ3])],"derivedFrom":makeQuery(id+"F1MoAnU7Y2teXVl_2.7.F4.boolean.opBoolean","SPLIT",FACE,{"disambiguationData":[TD([subQ3])],"derivedFrom":makeQuery(id+"F1MoAnU7Y2teXVl_2.6.F4.boolean.opBoolean","SPLIT",FACE,{"disambiguationData":[TD([subQ3])],"derivedFrom":makeQuery(id+"F1MoAnU7Y2teXVl_2.5.F4.boolean.opBoolean","SPLIT",FACE,{"disambiguationData":[TD([subQ3])],"derivedFrom":makeQuery(id+"F1MoAnU7Y2teXVl_2.4.F4.boolean.opBoolean","SPLIT",FACE,{"disambiguationData":[TD([subQ3])],"derivedFrom":makeQuery(id+"F1MoAnU7Y2teXVl_2.3.F4.boolean.opBoolean","SPLIT",FACE,{"disambiguationData":[TD([subQ3])],"derivedFrom":makeQuery(id+"F1MoAnU7Y2teXVl_2.2.F4.boolean.opBoolean","SPLIT",FACE,{"disambiguationData":[TD([subQ3])],"derivedFrom":makeQuery(id+"F1MoAnU7Y2teXVl_2.1.F4.boolean.opBoolean","SPLIT",FACE,{"disambiguationData":[TD([subQ3])],"derivedFrom":makeQuery(id+"F3.opRevolve","SWEPT_FACE",FACE,{"disambiguationData":[OSD([sQuery(id+"F0.wireOp",EDGE,"E30")])]})})})})})})})})})})})})}),makeQuery(id+"F1MoAnU7Y2teXVl_2.13.F4.opExtrude","SWEPT_FACE",FACE,{"disambiguationData":[OSD([subQ0])]})]});}
            var Q22;
            {var subQ0=sQuery(id+"F1.wireOp",EDGE,"E59");var subQ3=makeQuery(id+"F4.boolean.opBoolean","COPY",FACE,{"derivedFrom":makeQuery(id+"F4.opExtrude","SWEPT_FACE",FACE,{"disambiguationData":[OSD([sQuery(id+"F1.wireOp",EDGE,"E60")])]})});Q22=makeQuery(id+"F1MoAnU7Y2teXVl_2.12.F4.boolean.opBoolean","INTERSECT",EDGE,{"derivedFrom":[makeQuery(id+"F1MoAnU7Y2teXVl_2.11.F4.boolean.opBoolean","SPLIT",FACE,{"disambiguationData":[TD([subQ3])],"derivedFrom":makeQuery(id+"F1MoAnU7Y2teXVl_2.10.F4.boolean.opBoolean","SPLIT",FACE,{"disambiguationData":[TD([subQ3])],"derivedFrom":makeQuery(id+"F1MoAnU7Y2teXVl_2.9.F4.boolean.opBoolean","SPLIT",FACE,{"disambiguationData":[TD([subQ3])],"derivedFrom":makeQuery(id+"F1MoAnU7Y2teXVl_2.8.F4.boolean.opBoolean","SPLIT",FACE,{"disambiguationData":[TD([subQ3])],"derivedFrom":makeQuery(id+"F1MoAnU7Y2teXVl_2.7.F4.boolean.opBoolean","SPLIT",FACE,{"disambiguationData":[TD([subQ3])],"derivedFrom":makeQuery(id+"F1MoAnU7Y2teXVl_2.6.F4.boolean.opBoolean","SPLIT",FACE,{"disambiguationData":[TD([subQ3])],"derivedFrom":makeQuery(id+"F1MoAnU7Y2teXVl_2.5.F4.boolean.opBoolean","SPLIT",FACE,{"disambiguationData":[TD([subQ3])],"derivedFrom":makeQuery(id+"F1MoAnU7Y2teXVl_2.4.F4.boolean.opBoolean","SPLIT",FACE,{"disambiguationData":[TD([subQ3])],"derivedFrom":makeQuery(id+"F1MoAnU7Y2teXVl_2.3.F4.boolean.opBoolean","SPLIT",FACE,{"disambiguationData":[TD([subQ3])],"derivedFrom":makeQuery(id+"F1MoAnU7Y2teXVl_2.2.F4.boolean.opBoolean","SPLIT",FACE,{"disambiguationData":[TD([subQ3])],"derivedFrom":makeQuery(id+"F1MoAnU7Y2teXVl_2.1.F4.boolean.opBoolean","SPLIT",FACE,{"disambiguationData":[TD([subQ3])],"derivedFrom":makeQuery(id+"F3.opRevolve","SWEPT_FACE",FACE,{"disambiguationData":[OSD([sQuery(id+"F0.wireOp",EDGE,"E30")])]})})})})})})})})})})})}),makeQuery(id+"F1MoAnU7Y2teXVl_2.12.F4.opExtrude","SWEPT_FACE",FACE,{"disambiguationData":[OSD([subQ0])]})]});}
            var Q23;
            {var subQ0=sQuery(id+"F1.wireOp",EDGE,"E59");var subQ3=makeQuery(id+"F4.boolean.opBoolean","COPY",FACE,{"derivedFrom":makeQuery(id+"F4.opExtrude","SWEPT_FACE",FACE,{"disambiguationData":[OSD([sQuery(id+"F1.wireOp",EDGE,"E60")])]})});Q23=makeQuery(id+"F1MoAnU7Y2teXVl_2.11.F4.boolean.opBoolean","INTERSECT",EDGE,{"derivedFrom":[makeQuery(id+"F1MoAnU7Y2teXVl_2.10.F4.boolean.opBoolean","SPLIT",FACE,{"disambiguationData":[TD([subQ3])],"derivedFrom":makeQuery(id+"F1MoAnU7Y2teXVl_2.9.F4.boolean.opBoolean","SPLIT",FACE,{"disambiguationData":[TD([subQ3])],"derivedFrom":makeQuery(id+"F1MoAnU7Y2teXVl_2.8.F4.boolean.opBoolean","SPLIT",FACE,{"disambiguationData":[TD([subQ3])],"derivedFrom":makeQuery(id+"F1MoAnU7Y2teXVl_2.7.F4.boolean.opBoolean","SPLIT",FACE,{"disambiguationData":[TD([subQ3])],"derivedFrom":makeQuery(id+"F1MoAnU7Y2teXVl_2.6.F4.boolean.opBoolean","SPLIT",FACE,{"disambiguationData":[TD([subQ3])],"derivedFrom":makeQuery(id+"F1MoAnU7Y2teXVl_2.5.F4.boolean.opBoolean","SPLIT",FACE,{"disambiguationData":[TD([subQ3])],"derivedFrom":makeQuery(id+"F1MoAnU7Y2teXVl_2.4.F4.boolean.opBoolean","SPLIT",FACE,{"disambiguationData":[TD([subQ3])],"derivedFrom":makeQuery(id+"F1MoAnU7Y2teXVl_2.3.F4.boolean.opBoolean","SPLIT",FACE,{"disambiguationData":[TD([subQ3])],"derivedFrom":makeQuery(id+"F1MoAnU7Y2teXVl_2.2.F4.boolean.opBoolean","SPLIT",FACE,{"disambiguationData":[TD([subQ3])],"derivedFrom":makeQuery(id+"F1MoAnU7Y2teXVl_2.1.F4.boolean.opBoolean","SPLIT",FACE,{"disambiguationData":[TD([subQ3])],"derivedFrom":makeQuery(id+"F3.opRevolve","SWEPT_FACE",FACE,{"disambiguationData":[OSD([sQuery(id+"F0.wireOp",EDGE,"E30")])]})})})})})})})})})})}),makeQuery(id+"F1MoAnU7Y2teXVl_2.11.F4.opExtrude","SWEPT_FACE",FACE,{"disambiguationData":[OSD([subQ0])]})]});}
            var Q24;
            {var subQ0=sQuery(id+"F1.wireOp",EDGE,"E59");var subQ3=makeQuery(id+"F4.boolean.opBoolean","COPY",FACE,{"derivedFrom":makeQuery(id+"F4.opExtrude","SWEPT_FACE",FACE,{"disambiguationData":[OSD([sQuery(id+"F1.wireOp",EDGE,"E60")])]})});Q24=makeQuery(id+"F1MoAnU7Y2teXVl_2.10.F4.boolean.opBoolean","INTERSECT",EDGE,{"derivedFrom":[makeQuery(id+"F1MoAnU7Y2teXVl_2.9.F4.boolean.opBoolean","SPLIT",FACE,{"disambiguationData":[TD([subQ3])],"derivedFrom":makeQuery(id+"F1MoAnU7Y2teXVl_2.8.F4.boolean.opBoolean","SPLIT",FACE,{"disambiguationData":[TD([subQ3])],"derivedFrom":makeQuery(id+"F1MoAnU7Y2teXVl_2.7.F4.boolean.opBoolean","SPLIT",FACE,{"disambiguationData":[TD([subQ3])],"derivedFrom":makeQuery(id+"F1MoAnU7Y2teXVl_2.6.F4.boolean.opBoolean","SPLIT",FACE,{"disambiguationData":[TD([subQ3])],"derivedFrom":makeQuery(id+"F1MoAnU7Y2teXVl_2.5.F4.boolean.opBoolean","SPLIT",FACE,{"disambiguationData":[TD([subQ3])],"derivedFrom":makeQuery(id+"F1MoAnU7Y2teXVl_2.4.F4.boolean.opBoolean","SPLIT",FACE,{"disambiguationData":[TD([subQ3])],"derivedFrom":makeQuery(id+"F1MoAnU7Y2teXVl_2.3.F4.boolean.opBoolean","SPLIT",FACE,{"disambiguationData":[TD([subQ3])],"derivedFrom":makeQuery(id+"F1MoAnU7Y2teXVl_2.2.F4.boolean.opBoolean","SPLIT",FACE,{"disambiguationData":[TD([subQ3])],"derivedFrom":makeQuery(id+"F1MoAnU7Y2teXVl_2.1.F4.boolean.opBoolean","SPLIT",FACE,{"disambiguationData":[TD([subQ3])],"derivedFrom":makeQuery(id+"F3.opRevolve","SWEPT_FACE",FACE,{"disambiguationData":[OSD([sQuery(id+"F0.wireOp",EDGE,"E30")])]})})})})})})})})})}),makeQuery(id+"F1MoAnU7Y2teXVl_2.10.F4.opExtrude","SWEPT_FACE",FACE,{"disambiguationData":[OSD([subQ0])]})]});}
            var Q25;
            {var subQ0=sQuery(id+"F1.wireOp",EDGE,"E59");var subQ3=makeQuery(id+"F4.boolean.opBoolean","COPY",FACE,{"derivedFrom":makeQuery(id+"F4.opExtrude","SWEPT_FACE",FACE,{"disambiguationData":[OSD([sQuery(id+"F1.wireOp",EDGE,"E60")])]})});Q25=makeQuery(id+"F1MoAnU7Y2teXVl_2.9.F4.boolean.opBoolean","INTERSECT",EDGE,{"derivedFrom":[makeQuery(id+"F1MoAnU7Y2teXVl_2.8.F4.boolean.opBoolean","SPLIT",FACE,{"disambiguationData":[TD([subQ3])],"derivedFrom":makeQuery(id+"F1MoAnU7Y2teXVl_2.7.F4.boolean.opBoolean","SPLIT",FACE,{"disambiguationData":[TD([subQ3])],"derivedFrom":makeQuery(id+"F1MoAnU7Y2teXVl_2.6.F4.boolean.opBoolean","SPLIT",FACE,{"disambiguationData":[TD([subQ3])],"derivedFrom":makeQuery(id+"F1MoAnU7Y2teXVl_2.5.F4.boolean.opBoolean","SPLIT",FACE,{"disambiguationData":[TD([subQ3])],"derivedFrom":makeQuery(id+"F1MoAnU7Y2teXVl_2.4.F4.boolean.opBoolean","SPLIT",FACE,{"disambiguationData":[TD([subQ3])],"derivedFrom":makeQuery(id+"F1MoAnU7Y2teXVl_2.3.F4.boolean.opBoolean","SPLIT",FACE,{"disambiguationData":[TD([subQ3])],"derivedFrom":makeQuery(id+"F1MoAnU7Y2teXVl_2.2.F4.boolean.opBoolean","SPLIT",FACE,{"disambiguationData":[TD([subQ3])],"derivedFrom":makeQuery(id+"F1MoAnU7Y2teXVl_2.1.F4.boolean.opBoolean","SPLIT",FACE,{"disambiguationData":[TD([subQ3])],"derivedFrom":makeQuery(id+"F3.opRevolve","SWEPT_FACE",FACE,{"disambiguationData":[OSD([sQuery(id+"F0.wireOp",EDGE,"E30")])]})})})})})})})})}),makeQuery(id+"F1MoAnU7Y2teXVl_2.9.F4.opExtrude","SWEPT_FACE",FACE,{"disambiguationData":[OSD([subQ0])]})]});}
            var Q26;
            {var subQ0=sQuery(id+"F1.wireOp",EDGE,"E59");var subQ3=makeQuery(id+"F4.boolean.opBoolean","COPY",FACE,{"derivedFrom":makeQuery(id+"F4.opExtrude","SWEPT_FACE",FACE,{"disambiguationData":[OSD([sQuery(id+"F1.wireOp",EDGE,"E60")])]})});Q26=makeQuery(id+"F1MoAnU7Y2teXVl_2.8.F4.boolean.opBoolean","INTERSECT",EDGE,{"derivedFrom":[makeQuery(id+"F1MoAnU7Y2teXVl_2.7.F4.boolean.opBoolean","SPLIT",FACE,{"disambiguationData":[TD([subQ3])],"derivedFrom":makeQuery(id+"F1MoAnU7Y2teXVl_2.6.F4.boolean.opBoolean","SPLIT",FACE,{"disambiguationData":[TD([subQ3])],"derivedFrom":makeQuery(id+"F1MoAnU7Y2teXVl_2.5.F4.boolean.opBoolean","SPLIT",FACE,{"disambiguationData":[TD([subQ3])],"derivedFrom":makeQuery(id+"F1MoAnU7Y2teXVl_2.4.F4.boolean.opBoolean","SPLIT",FACE,{"disambiguationData":[TD([subQ3])],"derivedFrom":makeQuery(id+"F1MoAnU7Y2teXVl_2.3.F4.boolean.opBoolean","SPLIT",FACE,{"disambiguationData":[TD([subQ3])],"derivedFrom":makeQuery(id+"F1MoAnU7Y2teXVl_2.2.F4.boolean.opBoolean","SPLIT",FACE,{"disambiguationData":[TD([subQ3])],"derivedFrom":makeQuery(id+"F1MoAnU7Y2teXVl_2.1.F4.boolean.opBoolean","SPLIT",FACE,{"disambiguationData":[TD([subQ3])],"derivedFrom":makeQuery(id+"F3.opRevolve","SWEPT_FACE",FACE,{"disambiguationData":[OSD([sQuery(id+"F0.wireOp",EDGE,"E30")])]})})})})})})})}),makeQuery(id+"F1MoAnU7Y2teXVl_2.8.F4.opExtrude","SWEPT_FACE",FACE,{"disambiguationData":[OSD([subQ0])]})]});}
            var Q27;
            {var subQ0=sQuery(id+"F1.wireOp",EDGE,"E59");var subQ3=makeQuery(id+"F4.boolean.opBoolean","COPY",FACE,{"derivedFrom":makeQuery(id+"F4.opExtrude","SWEPT_FACE",FACE,{"disambiguationData":[OSD([sQuery(id+"F1.wireOp",EDGE,"E60")])]})});Q27=makeQuery(id+"F1MoAnU7Y2teXVl_2.7.F4.boolean.opBoolean","INTERSECT",EDGE,{"derivedFrom":[makeQuery(id+"F1MoAnU7Y2teXVl_2.6.F4.boolean.opBoolean","SPLIT",FACE,{"disambiguationData":[TD([subQ3])],"derivedFrom":makeQuery(id+"F1MoAnU7Y2teXVl_2.5.F4.boolean.opBoolean","SPLIT",FACE,{"disambiguationData":[TD([subQ3])],"derivedFrom":makeQuery(id+"F1MoAnU7Y2teXVl_2.4.F4.boolean.opBoolean","SPLIT",FACE,{"disambiguationData":[TD([subQ3])],"derivedFrom":makeQuery(id+"F1MoAnU7Y2teXVl_2.3.F4.boolean.opBoolean","SPLIT",FACE,{"disambiguationData":[TD([subQ3])],"derivedFrom":makeQuery(id+"F1MoAnU7Y2teXVl_2.2.F4.boolean.opBoolean","SPLIT",FACE,{"disambiguationData":[TD([subQ3])],"derivedFrom":makeQuery(id+"F1MoAnU7Y2teXVl_2.1.F4.boolean.opBoolean","SPLIT",FACE,{"disambiguationData":[TD([subQ3])],"derivedFrom":makeQuery(id+"F3.opRevolve","SWEPT_FACE",FACE,{"disambiguationData":[OSD([sQuery(id+"F0.wireOp",EDGE,"E30")])]})})})})})})}),makeQuery(id+"F1MoAnU7Y2teXVl_2.7.F4.opExtrude","SWEPT_FACE",FACE,{"disambiguationData":[OSD([subQ0])]})]});}
            var Q28;
            {var subQ0=sQuery(id+"F1.wireOp",EDGE,"E59");var subQ3=makeQuery(id+"F4.boolean.opBoolean","COPY",FACE,{"derivedFrom":makeQuery(id+"F4.opExtrude","SWEPT_FACE",FACE,{"disambiguationData":[OSD([sQuery(id+"F1.wireOp",EDGE,"E60")])]})});Q28=makeQuery(id+"F1MoAnU7Y2teXVl_2.6.F4.boolean.opBoolean","INTERSECT",EDGE,{"derivedFrom":[makeQuery(id+"F1MoAnU7Y2teXVl_2.5.F4.boolean.opBoolean","SPLIT",FACE,{"disambiguationData":[TD([subQ3])],"derivedFrom":makeQuery(id+"F1MoAnU7Y2teXVl_2.4.F4.boolean.opBoolean","SPLIT",FACE,{"disambiguationData":[TD([subQ3])],"derivedFrom":makeQuery(id+"F1MoAnU7Y2teXVl_2.3.F4.boolean.opBoolean","SPLIT",FACE,{"disambiguationData":[TD([subQ3])],"derivedFrom":makeQuery(id+"F1MoAnU7Y2teXVl_2.2.F4.boolean.opBoolean","SPLIT",FACE,{"disambiguationData":[TD([subQ3])],"derivedFrom":makeQuery(id+"F1MoAnU7Y2teXVl_2.1.F4.boolean.opBoolean","SPLIT",FACE,{"disambiguationData":[TD([subQ3])],"derivedFrom":makeQuery(id+"F3.opRevolve","SWEPT_FACE",FACE,{"disambiguationData":[OSD([sQuery(id+"F0.wireOp",EDGE,"E30")])]})})})})})}),makeQuery(id+"F1MoAnU7Y2teXVl_2.6.F4.opExtrude","SWEPT_FACE",FACE,{"disambiguationData":[OSD([subQ0])]})]});}
            var Q29;
            {var subQ0=sQuery(id+"F1.wireOp",EDGE,"E59");var subQ3=makeQuery(id+"F4.boolean.opBoolean","COPY",FACE,{"derivedFrom":makeQuery(id+"F4.opExtrude","SWEPT_FACE",FACE,{"disambiguationData":[OSD([sQuery(id+"F1.wireOp",EDGE,"E60")])]})});Q29=makeQuery(id+"F1MoAnU7Y2teXVl_2.5.F4.boolean.opBoolean","INTERSECT",EDGE,{"derivedFrom":[makeQuery(id+"F1MoAnU7Y2teXVl_2.4.F4.boolean.opBoolean","SPLIT",FACE,{"disambiguationData":[TD([subQ3])],"derivedFrom":makeQuery(id+"F1MoAnU7Y2teXVl_2.3.F4.boolean.opBoolean","SPLIT",FACE,{"disambiguationData":[TD([subQ3])],"derivedFrom":makeQuery(id+"F1MoAnU7Y2teXVl_2.2.F4.boolean.opBoolean","SPLIT",FACE,{"disambiguationData":[TD([subQ3])],"derivedFrom":makeQuery(id+"F1MoAnU7Y2teXVl_2.1.F4.boolean.opBoolean","SPLIT",FACE,{"disambiguationData":[TD([subQ3])],"derivedFrom":makeQuery(id+"F3.opRevolve","SWEPT_FACE",FACE,{"disambiguationData":[OSD([sQuery(id+"F0.wireOp",EDGE,"E30")])]})})})})}),makeQuery(id+"F1MoAnU7Y2teXVl_2.5.F4.opExtrude","SWEPT_FACE",FACE,{"disambiguationData":[OSD([subQ0])]})]});}
            var Q30;
            {var subQ0=sQuery(id+"F1.wireOp",EDGE,"E59");var subQ3=makeQuery(id+"F4.boolean.opBoolean","COPY",FACE,{"derivedFrom":makeQuery(id+"F4.opExtrude","SWEPT_FACE",FACE,{"disambiguationData":[OSD([sQuery(id+"F1.wireOp",EDGE,"E60")])]})});Q30=makeQuery(id+"F1MoAnU7Y2teXVl_2.4.F4.boolean.opBoolean","INTERSECT",EDGE,{"derivedFrom":[makeQuery(id+"F1MoAnU7Y2teXVl_2.3.F4.boolean.opBoolean","SPLIT",FACE,{"disambiguationData":[TD([subQ3])],"derivedFrom":makeQuery(id+"F1MoAnU7Y2teXVl_2.2.F4.boolean.opBoolean","SPLIT",FACE,{"disambiguationData":[TD([subQ3])],"derivedFrom":makeQuery(id+"F1MoAnU7Y2teXVl_2.1.F4.boolean.opBoolean","SPLIT",FACE,{"disambiguationData":[TD([subQ3])],"derivedFrom":makeQuery(id+"F3.opRevolve","SWEPT_FACE",FACE,{"disambiguationData":[OSD([sQuery(id+"F0.wireOp",EDGE,"E30")])]})})})}),makeQuery(id+"F1MoAnU7Y2teXVl_2.4.F4.opExtrude","SWEPT_FACE",FACE,{"disambiguationData":[OSD([subQ0])]})]});}
            var Q31;
            {var subQ0=sQuery(id+"F1.wireOp",EDGE,"E59");var subQ3=makeQuery(id+"F4.boolean.opBoolean","COPY",FACE,{"derivedFrom":makeQuery(id+"F4.opExtrude","SWEPT_FACE",FACE,{"disambiguationData":[OSD([sQuery(id+"F1.wireOp",EDGE,"E60")])]})});Q31=makeQuery(id+"F1MoAnU7Y2teXVl_2.3.F4.boolean.opBoolean","INTERSECT",EDGE,{"derivedFrom":[makeQuery(id+"F1MoAnU7Y2teXVl_2.2.F4.boolean.opBoolean","SPLIT",FACE,{"disambiguationData":[TD([subQ3])],"derivedFrom":makeQuery(id+"F1MoAnU7Y2teXVl_2.1.F4.boolean.opBoolean","SPLIT",FACE,{"disambiguationData":[TD([subQ3])],"derivedFrom":makeQuery(id+"F3.opRevolve","SWEPT_FACE",FACE,{"disambiguationData":[OSD([sQuery(id+"F0.wireOp",EDGE,"E30")])]})})}),makeQuery(id+"F1MoAnU7Y2teXVl_2.3.F4.opExtrude","SWEPT_FACE",FACE,{"disambiguationData":[OSD([subQ0])]})]});}
            fillet(context, id + "F5", {"entities" : qUnion([Q0, Q1, Q2, Q3, Q4, Q5, Q6, Q7, Q8, Q9, Q10, Q11, Q12, Q13, Q14, Q15, Q16, Q17, Q18, Q19, Q20, Q21, Q22, Q23, Q24, Q25, Q26, Q27, Q28, Q29, Q30, Q31]), "radius" : 2 * mm, "tangentPropagation" : true, "allowEdgeOverflow" : false});
        }
        {
            var Q0;
            {var subQ0=sQuery(id+"F0.wireOp",EDGE,"E2");var subQ2=sQuery(id+"F1.wireOp",EDGE,"E60");var subQ3=sQuery(id+"F0.wireOp",EDGE,"E29");var subQ5=sQuery(id+"F1.wireOp",EDGE,"E59");var subQ6=makeQuery(id+"F1MoAnU7Y2teXVl_2.8.F4.opExtrude","SWEPT_FACE",FACE,{"disambiguationData":[OSD([subQ5])]});var subQ7=makeQuery(id+"F4.boolean.opBoolean","COPY",FACE,{"derivedFrom":makeQuery(id+"F4.opExtrude","SWEPT_FACE",FACE,{"disambiguationData":[OSD([subQ2])]})});Q0=makeQuery(id+"F1MoAnU7Y2teXVl_2.9.F4.boolean.opBoolean","SPLIT",EDGE,{"disambiguationData":[TD([makeQuery(id+"F1MoAnU7Y2teXVl_2.8.F4.boolean.opBoolean","COPY",FACE,{"derivedFrom":subQ6})])],"derivedFrom":makeQuery(id+"F1MoAnU7Y2teXVl_2.8.F4.boolean.opBoolean","SPLIT",EDGE,{"disambiguationData":[TD([subQ7])],"derivedFrom":makeQuery(id+"F1MoAnU7Y2teXVl_2.7.F4.boolean.opBoolean","SPLIT",EDGE,{"disambiguationData":[TD([subQ7])],"derivedFrom":makeQuery(id+"F1MoAnU7Y2teXVl_2.6.F4.boolean.opBoolean","SPLIT",EDGE,{"disambiguationData":[TD([subQ7])],"derivedFrom":makeQuery(id+"F1MoAnU7Y2teXVl_2.5.F4.boolean.opBoolean","SPLIT",EDGE,{"disambiguationData":[TD([subQ7])],"derivedFrom":makeQuery(id+"F1MoAnU7Y2teXVl_2.4.F4.boolean.opBoolean","SPLIT",EDGE,{"disambiguationData":[TD([subQ7])],"derivedFrom":makeQuery(id+"F1MoAnU7Y2teXVl_2.3.F4.boolean.opBoolean","SPLIT",EDGE,{"disambiguationData":[TD([subQ7])],"derivedFrom":makeQuery(id+"F1MoAnU7Y2teXVl_2.2.F4.boolean.opBoolean","SPLIT",EDGE,{"disambiguationData":[TD([subQ7])],"derivedFrom":makeQuery(id+"F1MoAnU7Y2teXVl_2.1.F4.boolean.opBoolean","SPLIT",EDGE,{"disambiguationData":[TD([subQ7])],"derivedFrom":makeQuery(id+"F3.opRevolve","SWEPT_EDGE",EDGE,{"disambiguationData":[OSD([subQ0,subQ3])]})})})})})})})})})});}
            var Q1;
            {var subQ0=sQuery(id+"F0.wireOp",EDGE,"E2");var subQ2=sQuery(id+"F0.wireOp",EDGE,"E29");var subQ4=makeQuery(id+"F4.boolean.opBoolean","COPY",FACE,{"derivedFrom":makeQuery(id+"F4.opExtrude","SWEPT_FACE",FACE,{"disambiguationData":[OSD([sQuery(id+"F1.wireOp",EDGE,"E60")])]})});Q1=makeQuery(id+"F1MoAnU7Y2teXVl_2.9.F4.boolean.opBoolean","SPLIT",EDGE,{"disambiguationData":[TD([subQ4])],"derivedFrom":makeQuery(id+"F1MoAnU7Y2teXVl_2.8.F4.boolean.opBoolean","SPLIT",EDGE,{"disambiguationData":[TD([subQ4])],"derivedFrom":makeQuery(id+"F1MoAnU7Y2teXVl_2.7.F4.boolean.opBoolean","SPLIT",EDGE,{"disambiguationData":[TD([subQ4])],"derivedFrom":makeQuery(id+"F1MoAnU7Y2teXVl_2.6.F4.boolean.opBoolean","SPLIT",EDGE,{"disambiguationData":[TD([subQ4])],"derivedFrom":makeQuery(id+"F1MoAnU7Y2teXVl_2.5.F4.boolean.opBoolean","SPLIT",EDGE,{"disambiguationData":[TD([subQ4])],"derivedFrom":makeQuery(id+"F1MoAnU7Y2teXVl_2.4.F4.boolean.opBoolean","SPLIT",EDGE,{"disambiguationData":[TD([subQ4])],"derivedFrom":makeQuery(id+"F1MoAnU7Y2teXVl_2.3.F4.boolean.opBoolean","SPLIT",EDGE,{"disambiguationData":[TD([subQ4])],"derivedFrom":makeQuery(id+"F1MoAnU7Y2teXVl_2.2.F4.boolean.opBoolean","SPLIT",EDGE,{"disambiguationData":[TD([subQ4])],"derivedFrom":makeQuery(id+"F1MoAnU7Y2teXVl_2.1.F4.boolean.opBoolean","SPLIT",EDGE,{"disambiguationData":[TD([subQ4])],"derivedFrom":makeQuery(id+"F3.opRevolve","SWEPT_EDGE",EDGE,{"disambiguationData":[OSD([subQ0,subQ2])]})})})})})})})})})});}
            var Q2;
            {var subQ0=sQuery(id+"F0.wireOp",EDGE,"E2");var subQ1=sQuery(id+"F0.wireOp",EDGE,"E29");Q2=makeQuery(id+"F1MoAnU7Y2teXVl_2.1.F4.boolean.opBoolean","SPLIT",EDGE,{"disambiguationData":[TD([makeQuery(id+"F4.boolean.opBoolean","COPY",FACE,{"derivedFrom":makeQuery(id+"F4.opExtrude","SWEPT_FACE",FACE,{"disambiguationData":[OSD([sQuery(id+"F1.wireOp",EDGE,"E59")])]})})])],"derivedFrom":makeQuery(id+"F3.opRevolve","SWEPT_EDGE",EDGE,{"disambiguationData":[OSD([subQ0,subQ1])]})});}
            var Q3;
            {var subQ0=sQuery(id+"F0.wireOp",EDGE,"E2");var subQ2=sQuery(id+"F0.wireOp",EDGE,"E29");var subQ4=makeQuery(id+"F1MoAnU7Y2teXVl_2.1.F4.opExtrude","SWEPT_FACE",FACE,{"disambiguationData":[OSD([sQuery(id+"F1.wireOp",EDGE,"E59")])]});var subQ5=sQuery(id+"F1.wireOp",EDGE,"E60");Q3=makeQuery(id+"F1MoAnU7Y2teXVl_2.2.F4.boolean.opBoolean","SPLIT",EDGE,{"disambiguationData":[TD([makeQuery(id+"F1MoAnU7Y2teXVl_2.1.F4.boolean.opBoolean","COPY",FACE,{"derivedFrom":subQ4})])],"derivedFrom":makeQuery(id+"F1MoAnU7Y2teXVl_2.1.F4.boolean.opBoolean","SPLIT",EDGE,{"disambiguationData":[TD([makeQuery(id+"F4.boolean.opBoolean","COPY",FACE,{"derivedFrom":makeQuery(id+"F4.opExtrude","SWEPT_FACE",FACE,{"disambiguationData":[OSD([subQ5])]})})])],"derivedFrom":makeQuery(id+"F3.opRevolve","SWEPT_EDGE",EDGE,{"disambiguationData":[OSD([subQ0,subQ2])]})})});}
            var Q4;
            {var subQ0=sQuery(id+"F0.wireOp",EDGE,"E2");var subQ2=sQuery(id+"F0.wireOp",EDGE,"E29");var subQ4=sQuery(id+"F1.wireOp",EDGE,"E59");var subQ5=makeQuery(id+"F1MoAnU7Y2teXVl_2.2.F4.opExtrude","SWEPT_FACE",FACE,{"disambiguationData":[OSD([subQ4])]});var subQ6=sQuery(id+"F1.wireOp",EDGE,"E60");var subQ7=makeQuery(id+"F4.boolean.opBoolean","COPY",FACE,{"derivedFrom":makeQuery(id+"F4.opExtrude","SWEPT_FACE",FACE,{"disambiguationData":[OSD([subQ6])]})});Q4=makeQuery(id+"F1MoAnU7Y2teXVl_2.3.F4.boolean.opBoolean","SPLIT",EDGE,{"disambiguationData":[TD([makeQuery(id+"F1MoAnU7Y2teXVl_2.2.F4.boolean.opBoolean","COPY",FACE,{"derivedFrom":subQ5})])],"derivedFrom":makeQuery(id+"F1MoAnU7Y2teXVl_2.2.F4.boolean.opBoolean","SPLIT",EDGE,{"disambiguationData":[TD([subQ7])],"derivedFrom":makeQuery(id+"F1MoAnU7Y2teXVl_2.1.F4.boolean.opBoolean","SPLIT",EDGE,{"disambiguationData":[TD([subQ7])],"derivedFrom":makeQuery(id+"F3.opRevolve","SWEPT_EDGE",EDGE,{"disambiguationData":[OSD([subQ0,subQ2])]})})})});}
            var Q5;
            {var subQ0=sQuery(id+"F0.wireOp",EDGE,"E2");var subQ2=sQuery(id+"F0.wireOp",EDGE,"E29");var subQ4=sQuery(id+"F1.wireOp",EDGE,"E60");var subQ5=sQuery(id+"F1.wireOp",EDGE,"E59");var subQ6=makeQuery(id+"F1MoAnU7Y2teXVl_2.3.F4.opExtrude","SWEPT_FACE",FACE,{"disambiguationData":[OSD([subQ5])]});var subQ7=makeQuery(id+"F4.boolean.opBoolean","COPY",FACE,{"derivedFrom":makeQuery(id+"F4.opExtrude","SWEPT_FACE",FACE,{"disambiguationData":[OSD([subQ4])]})});Q5=makeQuery(id+"F1MoAnU7Y2teXVl_2.4.F4.boolean.opBoolean","SPLIT",EDGE,{"disambiguationData":[TD([makeQuery(id+"F1MoAnU7Y2teXVl_2.3.F4.boolean.opBoolean","COPY",FACE,{"derivedFrom":subQ6})])],"derivedFrom":makeQuery(id+"F1MoAnU7Y2teXVl_2.3.F4.boolean.opBoolean","SPLIT",EDGE,{"disambiguationData":[TD([subQ7])],"derivedFrom":makeQuery(id+"F1MoAnU7Y2teXVl_2.2.F4.boolean.opBoolean","SPLIT",EDGE,{"disambiguationData":[TD([subQ7])],"derivedFrom":makeQuery(id+"F1MoAnU7Y2teXVl_2.1.F4.boolean.opBoolean","SPLIT",EDGE,{"disambiguationData":[TD([subQ7])],"derivedFrom":makeQuery(id+"F3.opRevolve","SWEPT_EDGE",EDGE,{"disambiguationData":[OSD([subQ0,subQ2])]})})})})});}
            var Q6;
            {var subQ0=sQuery(id+"F0.wireOp",EDGE,"E2");var subQ2=sQuery(id+"F0.wireOp",EDGE,"E29");var subQ4=sQuery(id+"F1.wireOp",EDGE,"E59");var subQ5=makeQuery(id+"F1MoAnU7Y2teXVl_2.4.F4.opExtrude","SWEPT_FACE",FACE,{"disambiguationData":[OSD([subQ4])]});var subQ6=sQuery(id+"F1.wireOp",EDGE,"E60");var subQ7=makeQuery(id+"F4.boolean.opBoolean","COPY",FACE,{"derivedFrom":makeQuery(id+"F4.opExtrude","SWEPT_FACE",FACE,{"disambiguationData":[OSD([subQ6])]})});Q6=makeQuery(id+"F1MoAnU7Y2teXVl_2.5.F4.boolean.opBoolean","SPLIT",EDGE,{"disambiguationData":[TD([makeQuery(id+"F1MoAnU7Y2teXVl_2.4.F4.boolean.opBoolean","COPY",FACE,{"derivedFrom":subQ5})])],"derivedFrom":makeQuery(id+"F1MoAnU7Y2teXVl_2.4.F4.boolean.opBoolean","SPLIT",EDGE,{"disambiguationData":[TD([subQ7])],"derivedFrom":makeQuery(id+"F1MoAnU7Y2teXVl_2.3.F4.boolean.opBoolean","SPLIT",EDGE,{"disambiguationData":[TD([subQ7])],"derivedFrom":makeQuery(id+"F1MoAnU7Y2teXVl_2.2.F4.boolean.opBoolean","SPLIT",EDGE,{"disambiguationData":[TD([subQ7])],"derivedFrom":makeQuery(id+"F1MoAnU7Y2teXVl_2.1.F4.boolean.opBoolean","SPLIT",EDGE,{"disambiguationData":[TD([subQ7])],"derivedFrom":makeQuery(id+"F3.opRevolve","SWEPT_EDGE",EDGE,{"disambiguationData":[OSD([subQ0,subQ2])]})})})})})});}
            var Q7;
            {var subQ0=sQuery(id+"F0.wireOp",EDGE,"E2");var subQ2=sQuery(id+"F0.wireOp",EDGE,"E29");var subQ4=sQuery(id+"F1.wireOp",EDGE,"E59");var subQ5=makeQuery(id+"F1MoAnU7Y2teXVl_2.5.F4.opExtrude","SWEPT_FACE",FACE,{"disambiguationData":[OSD([subQ4])]});var subQ6=sQuery(id+"F1.wireOp",EDGE,"E60");var subQ7=makeQuery(id+"F4.boolean.opBoolean","COPY",FACE,{"derivedFrom":makeQuery(id+"F4.opExtrude","SWEPT_FACE",FACE,{"disambiguationData":[OSD([subQ6])]})});Q7=makeQuery(id+"F1MoAnU7Y2teXVl_2.6.F4.boolean.opBoolean","SPLIT",EDGE,{"disambiguationData":[TD([makeQuery(id+"F1MoAnU7Y2teXVl_2.5.F4.boolean.opBoolean","COPY",FACE,{"derivedFrom":subQ5})])],"derivedFrom":makeQuery(id+"F1MoAnU7Y2teXVl_2.5.F4.boolean.opBoolean","SPLIT",EDGE,{"disambiguationData":[TD([subQ7])],"derivedFrom":makeQuery(id+"F1MoAnU7Y2teXVl_2.4.F4.boolean.opBoolean","SPLIT",EDGE,{"disambiguationData":[TD([subQ7])],"derivedFrom":makeQuery(id+"F1MoAnU7Y2teXVl_2.3.F4.boolean.opBoolean","SPLIT",EDGE,{"disambiguationData":[TD([subQ7])],"derivedFrom":makeQuery(id+"F1MoAnU7Y2teXVl_2.2.F4.boolean.opBoolean","SPLIT",EDGE,{"disambiguationData":[TD([subQ7])],"derivedFrom":makeQuery(id+"F1MoAnU7Y2teXVl_2.1.F4.boolean.opBoolean","SPLIT",EDGE,{"disambiguationData":[TD([subQ7])],"derivedFrom":makeQuery(id+"F3.opRevolve","SWEPT_EDGE",EDGE,{"disambiguationData":[OSD([subQ0,subQ2])]})})})})})})});}
            var Q8;
            {var subQ0=sQuery(id+"F0.wireOp",EDGE,"E2");var subQ2=sQuery(id+"F1.wireOp",EDGE,"E60");var subQ3=sQuery(id+"F0.wireOp",EDGE,"E29");var subQ5=sQuery(id+"F1.wireOp",EDGE,"E59");var subQ6=makeQuery(id+"F1MoAnU7Y2teXVl_2.6.F4.opExtrude","SWEPT_FACE",FACE,{"disambiguationData":[OSD([subQ5])]});var subQ7=makeQuery(id+"F4.boolean.opBoolean","COPY",FACE,{"derivedFrom":makeQuery(id+"F4.opExtrude","SWEPT_FACE",FACE,{"disambiguationData":[OSD([subQ2])]})});Q8=makeQuery(id+"F1MoAnU7Y2teXVl_2.7.F4.boolean.opBoolean","SPLIT",EDGE,{"disambiguationData":[TD([makeQuery(id+"F1MoAnU7Y2teXVl_2.6.F4.boolean.opBoolean","COPY",FACE,{"derivedFrom":subQ6})])],"derivedFrom":makeQuery(id+"F1MoAnU7Y2teXVl_2.6.F4.boolean.opBoolean","SPLIT",EDGE,{"disambiguationData":[TD([subQ7])],"derivedFrom":makeQuery(id+"F1MoAnU7Y2teXVl_2.5.F4.boolean.opBoolean","SPLIT",EDGE,{"disambiguationData":[TD([subQ7])],"derivedFrom":makeQuery(id+"F1MoAnU7Y2teXVl_2.4.F4.boolean.opBoolean","SPLIT",EDGE,{"disambiguationData":[TD([subQ7])],"derivedFrom":makeQuery(id+"F1MoAnU7Y2teXVl_2.3.F4.boolean.opBoolean","SPLIT",EDGE,{"disambiguationData":[TD([subQ7])],"derivedFrom":makeQuery(id+"F1MoAnU7Y2teXVl_2.2.F4.boolean.opBoolean","SPLIT",EDGE,{"disambiguationData":[TD([subQ7])],"derivedFrom":makeQuery(id+"F1MoAnU7Y2teXVl_2.1.F4.boolean.opBoolean","SPLIT",EDGE,{"disambiguationData":[TD([subQ7])],"derivedFrom":makeQuery(id+"F3.opRevolve","SWEPT_EDGE",EDGE,{"disambiguationData":[OSD([subQ0,subQ3])]})})})})})})})});}
            var Q9;
            {var subQ0=sQuery(id+"F0.wireOp",EDGE,"E2");var subQ2=sQuery(id+"F1.wireOp",EDGE,"E59");var subQ3=makeQuery(id+"F1MoAnU7Y2teXVl_2.7.F4.opExtrude","SWEPT_FACE",FACE,{"disambiguationData":[OSD([subQ2])]});var subQ4=sQuery(id+"F0.wireOp",EDGE,"E29");var subQ6=sQuery(id+"F1.wireOp",EDGE,"E60");var subQ7=makeQuery(id+"F4.boolean.opBoolean","COPY",FACE,{"derivedFrom":makeQuery(id+"F4.opExtrude","SWEPT_FACE",FACE,{"disambiguationData":[OSD([subQ6])]})});Q9=makeQuery(id+"F1MoAnU7Y2teXVl_2.8.F4.boolean.opBoolean","SPLIT",EDGE,{"disambiguationData":[TD([makeQuery(id+"F1MoAnU7Y2teXVl_2.7.F4.boolean.opBoolean","COPY",FACE,{"derivedFrom":subQ3})])],"derivedFrom":makeQuery(id+"F1MoAnU7Y2teXVl_2.7.F4.boolean.opBoolean","SPLIT",EDGE,{"disambiguationData":[TD([subQ7])],"derivedFrom":makeQuery(id+"F1MoAnU7Y2teXVl_2.6.F4.boolean.opBoolean","SPLIT",EDGE,{"disambiguationData":[TD([subQ7])],"derivedFrom":makeQuery(id+"F1MoAnU7Y2teXVl_2.5.F4.boolean.opBoolean","SPLIT",EDGE,{"disambiguationData":[TD([subQ7])],"derivedFrom":makeQuery(id+"F1MoAnU7Y2teXVl_2.4.F4.boolean.opBoolean","SPLIT",EDGE,{"disambiguationData":[TD([subQ7])],"derivedFrom":makeQuery(id+"F1MoAnU7Y2teXVl_2.3.F4.boolean.opBoolean","SPLIT",EDGE,{"disambiguationData":[TD([subQ7])],"derivedFrom":makeQuery(id+"F1MoAnU7Y2teXVl_2.2.F4.boolean.opBoolean","SPLIT",EDGE,{"disambiguationData":[TD([subQ7])],"derivedFrom":makeQuery(id+"F1MoAnU7Y2teXVl_2.1.F4.boolean.opBoolean","SPLIT",EDGE,{"disambiguationData":[TD([subQ7])],"derivedFrom":makeQuery(id+"F3.opRevolve","SWEPT_EDGE",EDGE,{"disambiguationData":[OSD([subQ0,subQ4])]})})})})})})})})});}
            fillet(context, id + "F6", {"entities" : qUnion([Q0, Q1, Q2, Q3, Q4, Q5, Q6, Q7, Q8, Q9]), "radius" : 5 * mm, "tangentPropagation" : true, "allowEdgeOverflow" : false});
        }
        {
            var Q0;
            Q0=makeQuery(id+"F0.imprint","IMPRINT",FACE,{"disambiguationData":[TD([[makeQuery(id+"F0.imprint","IMPRINT",EDGE,{"derivedFrom":sQuery(id+"F0.wireOp",EDGE,"E21.0")}),1.0]])]});
            var Q1;
            {var subQ0=sQuery(id+"F0.wireOp",EDGE,"E42");Q1=makeQuery(id+"F0.imprint","IMPRINT",FACE,{"disambiguationData":[TD([[makeQuery(id+"F0.imprint","IMPRINT",EDGE,{"derivedFrom":subQ0}),1.0]])]});}
            var Q2;
            Q2=sQuery(id+"F0.wireOp",EDGE,"E28");
            revolve(context, id + "F7", {"entities" : qUnion([Q0, Q1]), "axis" : qUnion([Q2]), "revolveType" : RevolveType.FULL});
        }
    });
